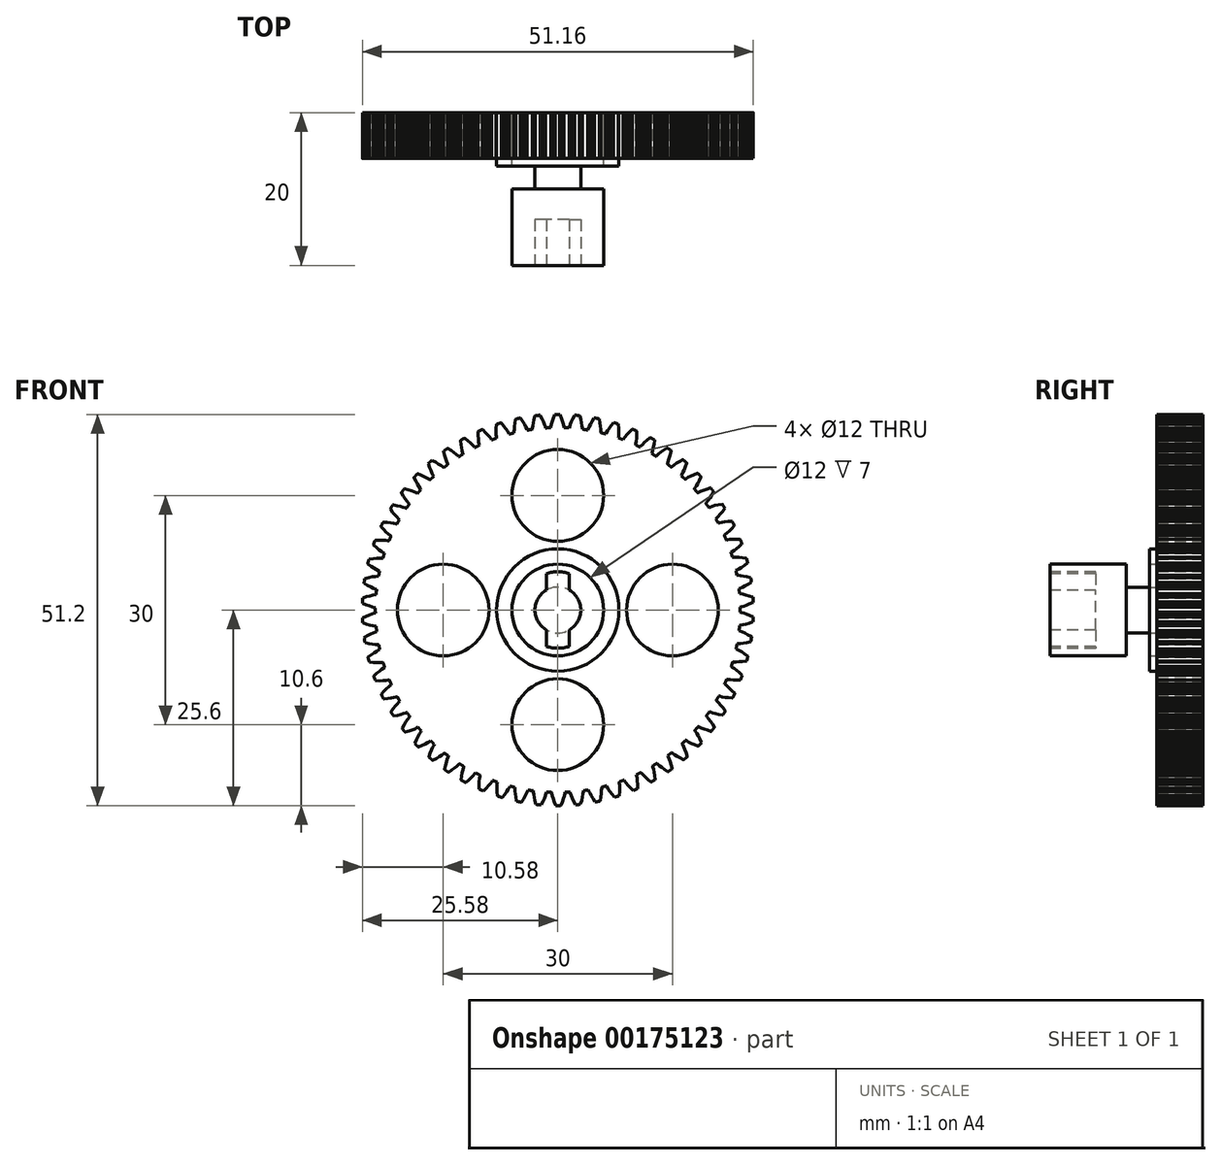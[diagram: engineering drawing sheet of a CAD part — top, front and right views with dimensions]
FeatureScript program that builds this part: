
annotation { "Feature Type Name" : "Feature", "Feature Type Description" : "" }
export const myFeature = defineFeature(function(context is Context, id is Id, definition is map)
    precondition{}
    {
        {
            var Q0;
            Q0=qCreatedBy(makeId("Front.planeOp"),FACE);
            var sketch = newSketch(context, id + "F0", { "sketchPlane" : qUnion([Q0])});
            skCircle(sketch, "E0", {"center": v(0, 0) * mm, "radius": 3 * mm});
            skCircle(sketch, "E1", {"center": v(0, 0) * mm, "radius": 6 * mm});
            skCircle(sketch, "E2", {"center": v(0, 0) * mm, "radius": 8 * mm});
            skSolve(sketch);
        }
        {
            var Q0;
            Q0=makeQuery(id+"F0.imprint","IMPRINT",FACE,{"disambiguationData":[TD([[makeQuery(id+"F0.imprint","IMPRINT",EDGE,{"derivedFrom":sQuery(id+"F0.wireOp",EDGE,"E0")}),-1.0]])]});
            var Q1;
            Q1=makeQuery(id+"F0.imprint","IMPRINT",FACE,{"disambiguationData":[TD([[makeQuery(id+"F0.imprint","IMPRINT",EDGE,{"derivedFrom":sQuery(id+"F0.wireOp",EDGE,"E0")}),1.0]])]});
            extrude(context, id + "F1", {"entities" : qUnion([Q0, Q1]), "depth" : 20 * mm});
        }
        {
            var Q0;
            Q0 = qSketchRegion(id + "F0", true);
            extrude(context, id + "F2", {"entities" : qUnion([Q0]), "operationType" : NewBodyOperationType.ADD, "depth" : 6 * mm});
        }
        {
            var Q0;
            Q0=makeQuery(id+"F0.imprint","IMPRINT",FACE,{"disambiguationData":[TD([[makeQuery(id+"F0.imprint","IMPRINT",EDGE,{"derivedFrom":sQuery(id+"F0.wireOp",EDGE,"E1")}),-1.0]])]});
            extrude(context, id + "F3", {"entities" : qUnion([Q0]), "operationType" : NewBodyOperationType.ADD, "depth" : 7 * mm});
        }
        {
            var Q0;
            Q0=makeQuery(id+"F1.opExtrude","CAP_FACE",FACE,{"disambiguationData":[OSD([sQuery(id+"F0.wireOp",EDGE,"E1")])],"isStart":false});
            var sketch = newSketch(context, id + "F4", { "sketchPlane" : qUnion([Q0])});
            skArc(sketch, "E3", {"start": v(-1.5, 2.6) * mm, "mid": v(-3, 0) * mm, "end": v(-1.5, -2.6) * mm});
            skLineSegment(sketch, "E4", {"start": v(-1.5, 4.77) * mm, "end": v(-1.5, 2.6) * mm});
            skLineSegment(sketch, "E5", {"start": v(1.5, 4.77) * mm, "end": v(1.5, 2.6) * mm});
            skArc(sketch, "E6.trimOffspring", {"start": v(1.5, -2.6) * mm, "mid": v(3, 0) * mm, "end": v(1.5, 2.6) * mm});
            skLineSegment(sketch, "E7.trimOffspring", {"start": v(-1.5, -2.6) * mm, "end": v(-1.5, -4.77) * mm});
            skLineSegment(sketch, "E8.trimOffspring", {"start": v(1.5, -2.6) * mm, "end": v(1.5, -4.77) * mm});
            skArc(sketch, "E9", {"start": v(-1.5, -4.77) * mm, "mid": v(0, -5) * mm, "end": v(1.5, -4.77) * mm});
            skArc(sketch, "E10.trimOffspring", {"start": v(1.5, 4.77) * mm, "mid": v(0, 5) * mm, "end": v(-1.5, 4.77) * mm});
            skSolve(sketch);
        }
        {
            var Q0;
            Q0=makeQuery(id+"F4.imprint","IMPRINT",FACE,{"disambiguationData":[TD([[makeQuery(id+"F4.imprint","IMPRINT",EDGE,{"derivedFrom":sQuery(id+"F4.wireOp",EDGE,"E3")}),1.0]])]});
            extrude(context, id + "F5", {"entities" : qUnion([Q0]), "operationType" : NewBodyOperationType.REMOVE, "oppositeDirection" : true, "depth" : 6 * mm});
        }
        {
            var Q0;
            Q0=qCreatedBy(makeId("Front.planeOp"),FACE);
            var sketch = newSketch(context, id + "F6", { "sketchPlane" : qUnion([Q0])});
            skLineSegment(sketch, "E11", {"start": v(18.3, 15.34) * mm, "end": v(18.43, 15.4) * mm});
            skLineSegment(sketch, "E12", {"start": v(18.43, 15.4) * mm, "end": v(18.72, 15.54) * mm});
            skLineSegment(sketch, "E13", {"start": v(18.72, 15.54) * mm, "end": v(19.07, 15.68) * mm});
            skLineSegment(sketch, "E14", {"start": v(19.07, 15.68) * mm, "end": v(19.49, 15.82) * mm});
            skLineSegment(sketch, "E15", {"start": v(19.49, 15.82) * mm, "end": v(19.96, 15.96) * mm});
            skLineSegment(sketch, "E16", {"start": v(19.96, 15.96) * mm, "end": v(20.01, 15.97) * mm});
            skArc(sketch, "E17", {"start": v(20.01, 15.97) * mm, "mid": v(20.2, 15.72) * mm, "end": v(20.4, 15.47) * mm});
            skLineSegment(sketch, "E18", {"start": v(20.4, 15.47) * mm, "end": v(20.38, 15.42) * mm});
            skLineSegment(sketch, "E19", {"start": v(20.38, 15.42) * mm, "end": v(20.13, 15) * mm});
            skLineSegment(sketch, "E20", {"start": v(20.13, 15) * mm, "end": v(19.9, 14.63) * mm});
            skLineSegment(sketch, "E21", {"start": v(19.9, 14.63) * mm, "end": v(19.67, 14.32) * mm});
            skLineSegment(sketch, "E22", {"start": v(19.67, 14.32) * mm, "end": v(19.47, 14.07) * mm});
            skLineSegment(sketch, "E23", {"start": v(19.47, 14.07) * mm, "end": v(19.37, 13.96) * mm});
            skArc(sketch, "E24", {"start": v(19.37, 13.96) * mm, "mid": v(19.56, 13.69) * mm, "end": v(19.75, 13.41) * mm});
            skLineSegment(sketch, "E25", {"start": v(19.75, 13.41) * mm, "end": v(19.9, 13.47) * mm});
            skLineSegment(sketch, "E26", {"start": v(19.9, 13.47) * mm, "end": v(20.2, 13.57) * mm});
            skLineSegment(sketch, "E27", {"start": v(20.2, 13.57) * mm, "end": v(20.56, 13.67) * mm});
            skLineSegment(sketch, "E28", {"start": v(20.56, 13.67) * mm, "end": v(20.99, 13.77) * mm});
            skLineSegment(sketch, "E29", {"start": v(20.99, 13.77) * mm, "end": v(21.47, 13.85) * mm});
            skLineSegment(sketch, "E30", {"start": v(21.47, 13.85) * mm, "end": v(21.52, 13.86) * mm});
            skArc(sketch, "E31", {"start": v(21.52, 13.86) * mm, "mid": v(21.7, 13.6) * mm, "end": v(21.86, 13.32) * mm});
            skLineSegment(sketch, "E32", {"start": v(21.86, 13.32) * mm, "end": v(21.83, 13.28) * mm});
            skLineSegment(sketch, "E33", {"start": v(21.83, 13.28) * mm, "end": v(21.54, 12.88) * mm});
            skLineSegment(sketch, "E34", {"start": v(21.54, 12.88) * mm, "end": v(21.27, 12.54) * mm});
            skLineSegment(sketch, "E35", {"start": v(21.27, 12.54) * mm, "end": v(21.02, 12.26) * mm});
            skLineSegment(sketch, "E36", {"start": v(21.02, 12.26) * mm, "end": v(20.8, 12.03) * mm});
            skLineSegment(sketch, "E37", {"start": v(20.8, 12.03) * mm, "end": v(20.68, 11.93) * mm});
            skArc(sketch, "E38", {"start": v(20.68, 11.93) * mm, "mid": v(20.85, 11.64) * mm, "end": v(21, 11.34) * mm});
            skLineSegment(sketch, "E39", {"start": v(21, 11.34) * mm, "end": v(21.15, 11.38) * mm});
            skLineSegment(sketch, "E40", {"start": v(21.15, 11.38) * mm, "end": v(21.46, 11.46) * mm});
            skLineSegment(sketch, "E41", {"start": v(21.46, 11.46) * mm, "end": v(21.84, 11.52) * mm});
            skLineSegment(sketch, "E42", {"start": v(21.84, 11.52) * mm, "end": v(22.27, 11.57) * mm});
            skLineSegment(sketch, "E43", {"start": v(22.27, 11.57) * mm, "end": v(22.77, 11.61) * mm});
            skLineSegment(sketch, "E44", {"start": v(22.77, 11.61) * mm, "end": v(22.81, 11.61) * mm});
            skArc(sketch, "E45", {"start": v(22.81, 11.61) * mm, "mid": v(22.96, 11.33) * mm, "end": v(23.1, 11.05) * mm});
            skLineSegment(sketch, "E46", {"start": v(23.1, 11.05) * mm, "end": v(23.06, 11) * mm});
            skLineSegment(sketch, "E47", {"start": v(23.06, 11) * mm, "end": v(22.73, 10.64) * mm});
            skLineSegment(sketch, "E48", {"start": v(22.73, 10.64) * mm, "end": v(22.43, 10.33) * mm});
            skLineSegment(sketch, "E49", {"start": v(22.43, 10.33) * mm, "end": v(22.15, 10.07) * mm});
            skLineSegment(sketch, "E50", {"start": v(22.15, 10.07) * mm, "end": v(21.9, 9.86) * mm});
            skLineSegment(sketch, "E51", {"start": v(21.9, 9.86) * mm, "end": v(21.78, 9.77) * mm});
            skArc(sketch, "E52", {"start": v(21.78, 9.77) * mm, "mid": v(21.92, 9.47) * mm, "end": v(22.05, 9.16) * mm});
            skLineSegment(sketch, "E53", {"start": v(22.05, 9.16) * mm, "end": v(22.2, 9.19) * mm});
            skLineSegment(sketch, "E54", {"start": v(22.2, 9.19) * mm, "end": v(22.51, 9.23) * mm});
            skLineSegment(sketch, "E55", {"start": v(22.51, 9.23) * mm, "end": v(22.9, 9.25) * mm});
            skLineSegment(sketch, "E56", {"start": v(22.9, 9.25) * mm, "end": v(23.33, 9.26) * mm});
            skLineSegment(sketch, "E57", {"start": v(23.33, 9.26) * mm, "end": v(23.82, 9.25) * mm});
            skLineSegment(sketch, "E58", {"start": v(23.82, 9.25) * mm, "end": v(23.87, 9.24) * mm});
            skArc(sketch, "E59", {"start": v(23.87, 9.24) * mm, "mid": v(23.98, 8.95) * mm, "end": v(24.1, 8.65) * mm});
            skLineSegment(sketch, "E60", {"start": v(24.1, 8.65) * mm, "end": v(24.06, 8.62) * mm});
            skLineSegment(sketch, "E61", {"start": v(24.06, 8.62) * mm, "end": v(23.7, 8.28) * mm});
            skLineSegment(sketch, "E62", {"start": v(23.7, 8.28) * mm, "end": v(23.36, 8) * mm});
            skLineSegment(sketch, "E63", {"start": v(23.36, 8) * mm, "end": v(23.05, 7.78) * mm});
            skLineSegment(sketch, "E64", {"start": v(23.05, 7.78) * mm, "end": v(22.79, 7.6) * mm});
            skLineSegment(sketch, "E65", {"start": v(22.79, 7.6) * mm, "end": v(22.66, 7.52) * mm});
            skArc(sketch, "E66", {"start": v(22.66, 7.52) * mm, "mid": v(22.76, 7.2) * mm, "end": v(22.86, 6.88) * mm});
            skLineSegment(sketch, "E67", {"start": v(22.86, 6.88) * mm, "end": v(23.01, 6.9) * mm});
            skLineSegment(sketch, "E68", {"start": v(23.01, 6.9) * mm, "end": v(23.33, 6.9) * mm});
            skLineSegment(sketch, "E69", {"start": v(23.33, 6.9) * mm, "end": v(23.7, 6.89) * mm});
            skLineSegment(sketch, "E70", {"start": v(23.7, 6.89) * mm, "end": v(24.15, 6.85) * mm});
            skLineSegment(sketch, "E71", {"start": v(24.15, 6.85) * mm, "end": v(24.64, 6.8) * mm});
            skLineSegment(sketch, "E72", {"start": v(24.64, 6.8) * mm, "end": v(24.69, 6.78) * mm});
            skArc(sketch, "E73", {"start": v(24.69, 6.78) * mm, "mid": v(24.77, 6.48) * mm, "end": v(24.85, 6.17) * mm});
            skLineSegment(sketch, "E74", {"start": v(24.85, 6.17) * mm, "end": v(24.8, 6.14) * mm});
            skLineSegment(sketch, "E75", {"start": v(24.8, 6.14) * mm, "end": v(24.41, 5.84) * mm});
            skLineSegment(sketch, "E76", {"start": v(24.41, 5.84) * mm, "end": v(24.05, 5.6) * mm});
            skLineSegment(sketch, "E77", {"start": v(24.05, 5.6) * mm, "end": v(23.72, 5.4) * mm});
            skLineSegment(sketch, "E78", {"start": v(23.72, 5.4) * mm, "end": v(23.44, 5.25) * mm});
            skLineSegment(sketch, "E79", {"start": v(23.44, 5.25) * mm, "end": v(23.3, 5.19) * mm});
            skArc(sketch, "E80", {"start": v(23.3, 5.19) * mm, "mid": v(23.37, 4.86) * mm, "end": v(23.44, 4.54) * mm});
            skLineSegment(sketch, "E81", {"start": v(23.44, 4.54) * mm, "end": v(23.6, 4.53) * mm});
            skLineSegment(sketch, "E82", {"start": v(23.6, 4.53) * mm, "end": v(23.9, 4.5) * mm});
            skLineSegment(sketch, "E83", {"start": v(23.9, 4.5) * mm, "end": v(24.29, 4.46) * mm});
            skLineSegment(sketch, "E84", {"start": v(24.29, 4.46) * mm, "end": v(24.72, 4.38) * mm});
            skLineSegment(sketch, "E85", {"start": v(24.72, 4.38) * mm, "end": v(25.2, 4.26) * mm});
            skLineSegment(sketch, "E86", {"start": v(25.2, 4.26) * mm, "end": v(25.24, 4.25) * mm});
            skArc(sketch, "E87", {"start": v(25.24, 4.25) * mm, "mid": v(25.3, 3.94) * mm, "end": v(25.34, 3.62) * mm});
            skLineSegment(sketch, "E88", {"start": v(25.34, 3.62) * mm, "end": v(25.3, 3.6) * mm});
            skLineSegment(sketch, "E89", {"start": v(25.3, 3.6) * mm, "end": v(24.88, 3.34) * mm});
            skLineSegment(sketch, "E90", {"start": v(24.88, 3.34) * mm, "end": v(24.5, 3.14) * mm});
            skLineSegment(sketch, "E91", {"start": v(24.5, 3.14) * mm, "end": v(24.15, 2.98) * mm});
            skLineSegment(sketch, "E92", {"start": v(24.15, 2.98) * mm, "end": v(23.85, 2.85) * mm});
            skLineSegment(sketch, "E93", {"start": v(23.85, 2.85) * mm, "end": v(23.7, 2.8) * mm});
            skArc(sketch, "E94", {"start": v(23.7, 2.8) * mm, "mid": v(23.75, 2.47) * mm, "end": v(23.78, 2.14) * mm});
            skLineSegment(sketch, "E95", {"start": v(23.78, 2.14) * mm, "end": v(23.93, 2.12) * mm});
            skLineSegment(sketch, "E96", {"start": v(23.93, 2.12) * mm, "end": v(24.24, 2.06) * mm});
            skLineSegment(sketch, "E97", {"start": v(24.24, 2.06) * mm, "end": v(24.61, 1.98) * mm});
            skLineSegment(sketch, "E98", {"start": v(24.61, 1.98) * mm, "end": v(25.03, 1.85) * mm});
            skLineSegment(sketch, "E99", {"start": v(25.03, 1.85) * mm, "end": v(25.5, 1.7) * mm});
            skLineSegment(sketch, "E100", {"start": v(25.5, 1.7) * mm, "end": v(25.55, 1.67) * mm});
            skArc(sketch, "E101", {"start": v(25.55, 1.67) * mm, "mid": v(25.56, 1.36) * mm, "end": v(25.58, 1.04) * mm});
            skLineSegment(sketch, "E102", {"start": v(25.58, 1.04) * mm, "end": v(25.53, 1.02) * mm});
            skLineSegment(sketch, "E103", {"start": v(25.53, 1.02) * mm, "end": v(25.09, 0.8) * mm});
            skLineSegment(sketch, "E104", {"start": v(25.09, 0.8) * mm, "end": v(24.68, 0.64) * mm});
            skLineSegment(sketch, "E105", {"start": v(24.68, 0.64) * mm, "end": v(24.32, 0.52) * mm});
            skLineSegment(sketch, "E106", {"start": v(24.32, 0.52) * mm, "end": v(24.02, 0.43) * mm});
            skLineSegment(sketch, "E107", {"start": v(24.02, 0.43) * mm, "end": v(23.87, 0.4) * mm});
            skArc(sketch, "E108", {"start": v(23.87, 0.4) * mm, "mid": v(23.87, 0.06) * mm, "end": v(23.87, -0.28) * mm});
            skLineSegment(sketch, "E109", {"start": v(23.87, -0.28) * mm, "end": v(24.02, -0.31) * mm});
            skLineSegment(sketch, "E110", {"start": v(24.02, -0.31) * mm, "end": v(24.33, -0.4) * mm});
            skLineSegment(sketch, "E111", {"start": v(24.33, -0.4) * mm, "end": v(24.68, -0.52) * mm});
            skLineSegment(sketch, "E112", {"start": v(24.68, -0.52) * mm, "end": v(25.1, -0.69) * mm});
            skLineSegment(sketch, "E113", {"start": v(25.1, -0.69) * mm, "end": v(25.54, -0.9) * mm});
            skLineSegment(sketch, "E114", {"start": v(25.54, -0.9) * mm, "end": v(25.58, -0.92) * mm});
            skArc(sketch, "E115", {"start": v(25.58, -0.92) * mm, "mid": v(25.57, -1.24) * mm, "end": v(25.55, -1.55) * mm});
            skLineSegment(sketch, "E116", {"start": v(25.55, -1.55) * mm, "end": v(25.5, -1.57) * mm});
            skLineSegment(sketch, "E117", {"start": v(25.5, -1.57) * mm, "end": v(25.04, -1.73) * mm});
            skLineSegment(sketch, "E118", {"start": v(25.04, -1.73) * mm, "end": v(24.62, -1.86) * mm});
            skLineSegment(sketch, "E119", {"start": v(24.62, -1.86) * mm, "end": v(24.25, -1.95) * mm});
            skLineSegment(sketch, "E120", {"start": v(24.25, -1.95) * mm, "end": v(23.94, -2) * mm});
            skLineSegment(sketch, "E121", {"start": v(23.94, -2) * mm, "end": v(23.79, -2.03) * mm});
            skArc(sketch, "E122", {"start": v(23.79, -2.03) * mm, "mid": v(23.76, -2.36) * mm, "end": v(23.72, -2.69) * mm});
            skLineSegment(sketch, "E123", {"start": v(23.72, -2.69) * mm, "end": v(23.86, -2.74) * mm});
            skLineSegment(sketch, "E124", {"start": v(23.86, -2.74) * mm, "end": v(24.16, -2.86) * mm});
            skLineSegment(sketch, "E125", {"start": v(24.16, -2.86) * mm, "end": v(24.5, -3.02) * mm});
            skLineSegment(sketch, "E126", {"start": v(24.5, -3.02) * mm, "end": v(24.9, -3.22) * mm});
            skLineSegment(sketch, "E127", {"start": v(24.9, -3.22) * mm, "end": v(25.32, -3.48) * mm});
            skLineSegment(sketch, "E128", {"start": v(25.32, -3.48) * mm, "end": v(25.36, -3.5) * mm});
            skArc(sketch, "E129", {"start": v(25.36, -3.5) * mm, "mid": v(25.31, -3.82) * mm, "end": v(25.27, -4.13) * mm});
            skLineSegment(sketch, "E130", {"start": v(25.27, -4.13) * mm, "end": v(25.22, -4.14) * mm});
            skLineSegment(sketch, "E131", {"start": v(25.22, -4.14) * mm, "end": v(24.74, -4.26) * mm});
            skLineSegment(sketch, "E132", {"start": v(24.74, -4.26) * mm, "end": v(24.3, -4.34) * mm});
            skLineSegment(sketch, "E133", {"start": v(24.3, -4.34) * mm, "end": v(23.93, -4.39) * mm});
            skLineSegment(sketch, "E134", {"start": v(23.93, -4.39) * mm, "end": v(23.61, -4.42) * mm});
            skLineSegment(sketch, "E135", {"start": v(23.61, -4.42) * mm, "end": v(23.46, -4.42) * mm});
            skArc(sketch, "E136", {"start": v(23.46, -4.42) * mm, "mid": v(23.4, -4.75) * mm, "end": v(23.33, -5.08) * mm});
            skLineSegment(sketch, "E137", {"start": v(23.33, -5.08) * mm, "end": v(23.47, -5.14) * mm});
            skLineSegment(sketch, "E138", {"start": v(23.47, -5.14) * mm, "end": v(23.75, -5.29) * mm});
            skLineSegment(sketch, "E139", {"start": v(23.75, -5.29) * mm, "end": v(24.07, -5.48) * mm});
            skLineSegment(sketch, "E140", {"start": v(24.07, -5.48) * mm, "end": v(24.44, -5.72) * mm});
            skLineSegment(sketch, "E141", {"start": v(24.44, -5.72) * mm, "end": v(24.84, -6.02) * mm});
            skLineSegment(sketch, "E142", {"start": v(24.84, -6.02) * mm, "end": v(24.87, -6.05) * mm});
            skArc(sketch, "E143", {"start": v(24.87, -6.05) * mm, "mid": v(24.8, -6.36) * mm, "end": v(24.72, -6.66) * mm});
            skLineSegment(sketch, "E144", {"start": v(24.72, -6.66) * mm, "end": v(24.67, -6.67) * mm});
            skLineSegment(sketch, "E145", {"start": v(24.67, -6.67) * mm, "end": v(24.18, -6.74) * mm});
            skLineSegment(sketch, "E146", {"start": v(24.18, -6.74) * mm, "end": v(23.74, -6.77) * mm});
            skLineSegment(sketch, "E147", {"start": v(23.74, -6.77) * mm, "end": v(23.36, -6.79) * mm});
            skLineSegment(sketch, "E148", {"start": v(23.36, -6.79) * mm, "end": v(23.04, -6.78) * mm});
            skLineSegment(sketch, "E149", {"start": v(23.04, -6.78) * mm, "end": v(22.9, -6.77) * mm});
            skArc(sketch, "E150", {"start": v(22.9, -6.77) * mm, "mid": v(22.8, -7.1) * mm, "end": v(22.7, -7.41) * mm});
            skLineSegment(sketch, "E151", {"start": v(22.7, -7.41) * mm, "end": v(22.82, -7.49) * mm});
            skLineSegment(sketch, "E152", {"start": v(22.82, -7.49) * mm, "end": v(23.1, -7.67) * mm});
            skLineSegment(sketch, "E153", {"start": v(23.1, -7.67) * mm, "end": v(23.4, -7.9) * mm});
            skLineSegment(sketch, "E154", {"start": v(23.4, -7.9) * mm, "end": v(23.73, -8.17) * mm});
            skLineSegment(sketch, "E155", {"start": v(23.73, -8.17) * mm, "end": v(24.1, -8.5) * mm});
            skLineSegment(sketch, "E156", {"start": v(24.1, -8.5) * mm, "end": v(24.14, -8.54) * mm});
            skArc(sketch, "E157", {"start": v(24.14, -8.54) * mm, "mid": v(24.03, -8.83) * mm, "end": v(23.92, -9.13) * mm});
            skLineSegment(sketch, "E158", {"start": v(23.92, -9.13) * mm, "end": v(23.87, -9.13) * mm});
            skLineSegment(sketch, "E159", {"start": v(23.87, -9.13) * mm, "end": v(23.37, -9.15) * mm});
            skLineSegment(sketch, "E160", {"start": v(23.37, -9.15) * mm, "end": v(22.94, -9.14) * mm});
            skLineSegment(sketch, "E161", {"start": v(22.94, -9.14) * mm, "end": v(22.56, -9.12) * mm});
            skLineSegment(sketch, "E162", {"start": v(22.56, -9.12) * mm, "end": v(22.24, -9.08) * mm});
            skLineSegment(sketch, "E163", {"start": v(22.24, -9.08) * mm, "end": v(22.1, -9.05) * mm});
            skArc(sketch, "E164", {"start": v(22.1, -9.05) * mm, "mid": v(21.96, -9.36) * mm, "end": v(21.83, -9.67) * mm});
            skLineSegment(sketch, "E165", {"start": v(21.83, -9.67) * mm, "end": v(21.95, -9.76) * mm});
            skLineSegment(sketch, "E166", {"start": v(21.95, -9.76) * mm, "end": v(22.2, -9.96) * mm});
            skLineSegment(sketch, "E167", {"start": v(22.2, -9.96) * mm, "end": v(22.48, -10.22) * mm});
            skLineSegment(sketch, "E168", {"start": v(22.48, -10.22) * mm, "end": v(22.79, -10.53) * mm});
            skLineSegment(sketch, "E169", {"start": v(22.79, -10.53) * mm, "end": v(23.12, -10.9) * mm});
            skLineSegment(sketch, "E170", {"start": v(23.12, -10.9) * mm, "end": v(23.15, -10.93) * mm});
            skArc(sketch, "E171", {"start": v(23.15, -10.93) * mm, "mid": v(23.01, -11.22) * mm, "end": v(22.87, -11.5) * mm});
            skLineSegment(sketch, "E172", {"start": v(22.87, -11.5) * mm, "end": v(22.82, -11.5) * mm});
            skLineSegment(sketch, "E173", {"start": v(22.82, -11.5) * mm, "end": v(22.33, -11.47) * mm});
            skLineSegment(sketch, "E174", {"start": v(22.33, -11.47) * mm, "end": v(21.9, -11.42) * mm});
            skLineSegment(sketch, "E175", {"start": v(21.9, -11.42) * mm, "end": v(21.52, -11.35) * mm});
            skLineSegment(sketch, "E176", {"start": v(21.52, -11.35) * mm, "end": v(21.2, -11.28) * mm});
            skLineSegment(sketch, "E177", {"start": v(21.2, -11.28) * mm, "end": v(21.06, -11.24) * mm});
            skArc(sketch, "E178", {"start": v(21.06, -11.24) * mm, "mid": v(20.9, -11.54) * mm, "end": v(20.74, -11.83) * mm});
            skLineSegment(sketch, "E179", {"start": v(20.74, -11.83) * mm, "end": v(20.85, -11.93) * mm});
            skLineSegment(sketch, "E180", {"start": v(20.85, -11.93) * mm, "end": v(21.08, -12.16) * mm});
            skLineSegment(sketch, "E181", {"start": v(21.08, -12.16) * mm, "end": v(21.33, -12.44) * mm});
            skLineSegment(sketch, "E182", {"start": v(21.33, -12.44) * mm, "end": v(21.6, -12.78) * mm});
            skLineSegment(sketch, "E183", {"start": v(21.6, -12.78) * mm, "end": v(21.9, -13.18) * mm});
            skLineSegment(sketch, "E184", {"start": v(21.9, -13.18) * mm, "end": v(21.92, -13.22) * mm});
            skArc(sketch, "E185", {"start": v(21.92, -13.22) * mm, "mid": v(21.76, -13.49) * mm, "end": v(21.59, -13.76) * mm});
            skLineSegment(sketch, "E186", {"start": v(21.59, -13.76) * mm, "end": v(21.54, -13.75) * mm});
            skLineSegment(sketch, "E187", {"start": v(21.54, -13.75) * mm, "end": v(21.05, -13.67) * mm});
            skLineSegment(sketch, "E188", {"start": v(21.05, -13.67) * mm, "end": v(20.63, -13.57) * mm});
            skLineSegment(sketch, "E189", {"start": v(20.63, -13.57) * mm, "end": v(20.26, -13.47) * mm});
            skLineSegment(sketch, "E190", {"start": v(20.26, -13.47) * mm, "end": v(19.96, -13.37) * mm});
            skLineSegment(sketch, "E191", {"start": v(19.96, -13.37) * mm, "end": v(19.82, -13.32) * mm});
            skArc(sketch, "E192", {"start": v(19.82, -13.32) * mm, "mid": v(19.63, -13.6) * mm, "end": v(19.44, -13.86) * mm});
            skLineSegment(sketch, "E193", {"start": v(19.44, -13.86) * mm, "end": v(19.54, -13.98) * mm});
            skLineSegment(sketch, "E194", {"start": v(19.54, -13.98) * mm, "end": v(19.74, -14.23) * mm});
            skLineSegment(sketch, "E195", {"start": v(19.74, -14.23) * mm, "end": v(19.96, -14.53) * mm});
            skLineSegment(sketch, "E196", {"start": v(19.96, -14.53) * mm, "end": v(20.2, -14.9) * mm});
            skLineSegment(sketch, "E197", {"start": v(20.2, -14.9) * mm, "end": v(20.45, -15.33) * mm});
            skLineSegment(sketch, "E198", {"start": v(20.45, -15.33) * mm, "end": v(20.47, -15.37) * mm});
            skArc(sketch, "E199", {"start": v(20.47, -15.37) * mm, "mid": v(20.28, -15.62) * mm, "end": v(20.09, -15.87) * mm});
            skLineSegment(sketch, "E200", {"start": v(20.09, -15.87) * mm, "end": v(20.04, -15.86) * mm});
            skLineSegment(sketch, "E201", {"start": v(20.04, -15.86) * mm, "end": v(19.56, -15.73) * mm});
            skLineSegment(sketch, "E202", {"start": v(19.56, -15.73) * mm, "end": v(19.15, -15.59) * mm});
            skLineSegment(sketch, "E203", {"start": v(19.15, -15.59) * mm, "end": v(18.8, -15.45) * mm});
            skLineSegment(sketch, "E204", {"start": v(18.8, -15.45) * mm, "end": v(18.5, -15.32) * mm});
            skLineSegment(sketch, "E205", {"start": v(18.5, -15.32) * mm, "end": v(18.37, -15.25) * mm});
            skArc(sketch, "E206", {"start": v(18.37, -15.25) * mm, "mid": v(18.15, -15.5) * mm, "end": v(17.93, -15.76) * mm});
            skLineSegment(sketch, "E207", {"start": v(17.93, -15.76) * mm, "end": v(18.02, -15.88) * mm});
            skLineSegment(sketch, "E208", {"start": v(18.02, -15.88) * mm, "end": v(18.2, -16.15) * mm});
            skLineSegment(sketch, "E209", {"start": v(18.2, -16.15) * mm, "end": v(18.39, -16.48) * mm});
            skLineSegment(sketch, "E210", {"start": v(18.39, -16.48) * mm, "end": v(18.59, -16.87) * mm});
            skLineSegment(sketch, "E211", {"start": v(18.59, -16.87) * mm, "end": v(18.8, -17.32) * mm});
            skLineSegment(sketch, "E212", {"start": v(18.8, -17.32) * mm, "end": v(18.81, -17.36) * mm});
            skArc(sketch, "E213", {"start": v(18.81, -17.36) * mm, "mid": v(18.6, -17.6) * mm, "end": v(18.38, -17.82) * mm});
            skLineSegment(sketch, "E214", {"start": v(18.38, -17.82) * mm, "end": v(18.33, -17.8) * mm});
            skLineSegment(sketch, "E215", {"start": v(18.33, -17.8) * mm, "end": v(17.87, -17.63) * mm});
            skLineSegment(sketch, "E216", {"start": v(17.87, -17.63) * mm, "end": v(17.47, -17.45) * mm});
            skLineSegment(sketch, "E217", {"start": v(17.47, -17.45) * mm, "end": v(17.13, -17.27) * mm});
            skLineSegment(sketch, "E218", {"start": v(17.13, -17.27) * mm, "end": v(16.86, -17.11) * mm});
            skLineSegment(sketch, "E219", {"start": v(16.86, -17.11) * mm, "end": v(16.73, -17.03) * mm});
            skArc(sketch, "E220", {"start": v(16.73, -17.03) * mm, "mid": v(16.5, -17.26) * mm, "end": v(16.25, -17.5) * mm});
            skLineSegment(sketch, "E221", {"start": v(16.25, -17.5) * mm, "end": v(16.32, -17.62) * mm});
            skLineSegment(sketch, "E222", {"start": v(16.32, -17.62) * mm, "end": v(16.47, -17.9) * mm});
            skLineSegment(sketch, "E223", {"start": v(16.47, -17.9) * mm, "end": v(16.63, -18.25) * mm});
            skLineSegment(sketch, "E224", {"start": v(16.63, -18.25) * mm, "end": v(16.79, -18.66) * mm});
            skLineSegment(sketch, "E225", {"start": v(16.79, -18.66) * mm, "end": v(16.95, -19.13) * mm});
            skLineSegment(sketch, "E226", {"start": v(16.95, -19.13) * mm, "end": v(16.96, -19.18) * mm});
            skArc(sketch, "E227", {"start": v(16.96, -19.18) * mm, "mid": v(16.72, -19.38) * mm, "end": v(16.48, -19.59) * mm});
            skLineSegment(sketch, "E228", {"start": v(16.48, -19.59) * mm, "end": v(16.44, -19.57) * mm});
            skLineSegment(sketch, "E229", {"start": v(16.44, -19.57) * mm, "end": v(16, -19.34) * mm});
            skLineSegment(sketch, "E230", {"start": v(16, -19.34) * mm, "end": v(15.62, -19.12) * mm});
            skLineSegment(sketch, "E231", {"start": v(15.62, -19.12) * mm, "end": v(15.3, -18.92) * mm});
            skLineSegment(sketch, "E232", {"start": v(15.3, -18.92) * mm, "end": v(15.04, -18.73) * mm});
            skLineSegment(sketch, "E233", {"start": v(15.04, -18.73) * mm, "end": v(14.92, -18.64) * mm});
            skArc(sketch, "E234", {"start": v(14.92, -18.64) * mm, "mid": v(14.66, -18.84) * mm, "end": v(14.4, -19.05) * mm});
            skLineSegment(sketch, "E235", {"start": v(14.4, -19.05) * mm, "end": v(14.46, -19.18) * mm});
            skLineSegment(sketch, "E236", {"start": v(14.46, -19.18) * mm, "end": v(14.57, -19.48) * mm});
            skLineSegment(sketch, "E237", {"start": v(14.57, -19.48) * mm, "end": v(14.7, -19.84) * mm});
            skLineSegment(sketch, "E238", {"start": v(14.7, -19.84) * mm, "end": v(14.81, -20.26) * mm});
            skLineSegment(sketch, "E239", {"start": v(14.81, -20.26) * mm, "end": v(14.92, -20.74) * mm});
            skLineSegment(sketch, "E240", {"start": v(14.92, -20.74) * mm, "end": v(14.93, -20.8) * mm});
            skArc(sketch, "E241", {"start": v(14.93, -20.8) * mm, "mid": v(14.68, -20.98) * mm, "end": v(14.41, -21.16) * mm});
            skLineSegment(sketch, "E242", {"start": v(14.41, -21.16) * mm, "end": v(14.37, -21.13) * mm});
            skLineSegment(sketch, "E243", {"start": v(14.37, -21.13) * mm, "end": v(13.96, -20.86) * mm});
            skLineSegment(sketch, "E244", {"start": v(13.96, -20.86) * mm, "end": v(13.6, -20.6) * mm});
            skLineSegment(sketch, "E245", {"start": v(13.6, -20.6) * mm, "end": v(13.3, -20.37) * mm});
            skLineSegment(sketch, "E246", {"start": v(13.3, -20.37) * mm, "end": v(13.07, -20.16) * mm});
            skLineSegment(sketch, "E247", {"start": v(13.07, -20.16) * mm, "end": v(12.96, -20.05) * mm});
            skArc(sketch, "E248", {"start": v(12.96, -20.05) * mm, "mid": v(12.68, -20.23) * mm, "end": v(12.4, -20.4) * mm});
            skLineSegment(sketch, "E249", {"start": v(12.4, -20.4) * mm, "end": v(12.44, -20.55) * mm});
            skLineSegment(sketch, "E250", {"start": v(12.44, -20.55) * mm, "end": v(12.53, -20.86) * mm});
            skLineSegment(sketch, "E251", {"start": v(12.53, -20.86) * mm, "end": v(12.61, -21.23) * mm});
            skLineSegment(sketch, "E252", {"start": v(12.61, -21.23) * mm, "end": v(12.69, -21.66) * mm});
            skLineSegment(sketch, "E253", {"start": v(12.69, -21.66) * mm, "end": v(12.75, -22.15) * mm});
            skLineSegment(sketch, "E254", {"start": v(12.75, -22.15) * mm, "end": v(12.75, -22.2) * mm});
            skArc(sketch, "E255", {"start": v(12.75, -22.2) * mm, "mid": v(12.48, -22.35) * mm, "end": v(12.2, -22.5) * mm});
            skLineSegment(sketch, "E256", {"start": v(12.2, -22.5) * mm, "end": v(12.16, -22.48) * mm});
            skLineSegment(sketch, "E257", {"start": v(12.16, -22.48) * mm, "end": v(11.77, -22.17) * mm});
            skLineSegment(sketch, "E258", {"start": v(11.77, -22.17) * mm, "end": v(11.45, -21.88) * mm});
            skLineSegment(sketch, "E259", {"start": v(11.45, -21.88) * mm, "end": v(11.18, -21.61) * mm});
            skLineSegment(sketch, "E260", {"start": v(11.18, -21.61) * mm, "end": v(10.96, -21.38) * mm});
            skLineSegment(sketch, "E261", {"start": v(10.96, -21.38) * mm, "end": v(10.86, -21.26) * mm});
            skArc(sketch, "E262", {"start": v(10.86, -21.26) * mm, "mid": v(10.57, -21.4) * mm, "end": v(10.27, -21.55) * mm});
            skLineSegment(sketch, "E263", {"start": v(10.27, -21.55) * mm, "end": v(10.3, -21.7) * mm});
            skLineSegment(sketch, "E264", {"start": v(10.3, -21.7) * mm, "end": v(10.35, -22.02) * mm});
            skLineSegment(sketch, "E265", {"start": v(10.35, -22.02) * mm, "end": v(10.4, -22.4) * mm});
            skLineSegment(sketch, "E266", {"start": v(10.4, -22.4) * mm, "end": v(10.43, -22.83) * mm});
            skLineSegment(sketch, "E267", {"start": v(10.43, -22.83) * mm, "end": v(10.44, -23.32) * mm});
            skLineSegment(sketch, "E268", {"start": v(10.44, -23.32) * mm, "end": v(10.44, -23.37) * mm});
            skArc(sketch, "E269", {"start": v(10.44, -23.37) * mm, "mid": v(10.15, -23.5) * mm, "end": v(9.86, -23.62) * mm});
            skLineSegment(sketch, "E270", {"start": v(9.86, -23.62) * mm, "end": v(9.82, -23.6) * mm});
            skLineSegment(sketch, "E271", {"start": v(9.82, -23.6) * mm, "end": v(9.47, -23.24) * mm});
            skLineSegment(sketch, "E272", {"start": v(9.47, -23.24) * mm, "end": v(9.18, -22.92) * mm});
            skLineSegment(sketch, "E273", {"start": v(9.18, -22.92) * mm, "end": v(8.93, -22.63) * mm});
            skLineSegment(sketch, "E274", {"start": v(8.93, -22.63) * mm, "end": v(8.74, -22.37) * mm});
            skLineSegment(sketch, "E275", {"start": v(8.74, -22.37) * mm, "end": v(8.66, -22.25) * mm});
            skArc(sketch, "E276", {"start": v(8.66, -22.25) * mm, "mid": v(8.35, -22.37) * mm, "end": v(8.03, -22.48) * mm});
            skLineSegment(sketch, "E277", {"start": v(8.03, -22.48) * mm, "end": v(8.05, -22.63) * mm});
            skLineSegment(sketch, "E278", {"start": v(8.05, -22.63) * mm, "end": v(8.07, -22.95) * mm});
            skLineSegment(sketch, "E279", {"start": v(8.07, -22.95) * mm, "end": v(8.08, -23.33) * mm});
            skLineSegment(sketch, "E280", {"start": v(8.08, -23.33) * mm, "end": v(8.07, -23.77) * mm});
            skLineSegment(sketch, "E281", {"start": v(8.07, -23.77) * mm, "end": v(8.03, -24.26) * mm});
            skLineSegment(sketch, "E282", {"start": v(8.03, -24.26) * mm, "end": v(8.02, -24.31) * mm});
            skArc(sketch, "E283", {"start": v(8.02, -24.31) * mm, "mid": v(7.72, -24.4) * mm, "end": v(7.42, -24.5) * mm});
            skLineSegment(sketch, "E284", {"start": v(7.42, -24.5) * mm, "end": v(7.39, -24.46) * mm});
            skLineSegment(sketch, "E285", {"start": v(7.39, -24.46) * mm, "end": v(7.07, -24.08) * mm});
            skLineSegment(sketch, "E286", {"start": v(7.07, -24.08) * mm, "end": v(6.8, -23.73) * mm});
            skLineSegment(sketch, "E287", {"start": v(6.8, -23.73) * mm, "end": v(6.6, -23.42) * mm});
            skLineSegment(sketch, "E288", {"start": v(6.6, -23.42) * mm, "end": v(6.43, -23.14) * mm});
            skLineSegment(sketch, "E289", {"start": v(6.43, -23.14) * mm, "end": v(6.36, -23.01) * mm});
            skArc(sketch, "E290", {"start": v(6.36, -23.01) * mm, "mid": v(6.04, -23.1) * mm, "end": v(5.72, -23.18) * mm});
            skLineSegment(sketch, "E291", {"start": v(5.72, -23.18) * mm, "end": v(5.72, -23.33) * mm});
            skLineSegment(sketch, "E292", {"start": v(5.72, -23.33) * mm, "end": v(5.7, -23.65) * mm});
            skLineSegment(sketch, "E293", {"start": v(5.7, -23.65) * mm, "end": v(5.68, -24.03) * mm});
            skLineSegment(sketch, "E294", {"start": v(5.68, -24.03) * mm, "end": v(5.62, -24.46) * mm});
            skLineSegment(sketch, "E295", {"start": v(5.62, -24.46) * mm, "end": v(5.53, -24.95) * mm});
            skLineSegment(sketch, "E296", {"start": v(5.53, -24.95) * mm, "end": v(5.52, -25) * mm});
            skArc(sketch, "E297", {"start": v(5.52, -25) * mm, "mid": v(5.21, -25.06) * mm, "end": v(4.9, -25.13) * mm});
            skLineSegment(sketch, "E298", {"start": v(4.9, -25.13) * mm, "end": v(4.87, -25.09) * mm});
            skLineSegment(sketch, "E299", {"start": v(4.87, -25.09) * mm, "end": v(4.6, -24.67) * mm});
            skLineSegment(sketch, "E300", {"start": v(4.6, -24.67) * mm, "end": v(4.37, -24.3) * mm});
            skLineSegment(sketch, "E301", {"start": v(4.37, -24.3) * mm, "end": v(4.2, -23.97) * mm});
            skLineSegment(sketch, "E302", {"start": v(4.2, -23.97) * mm, "end": v(4.06, -23.68) * mm});
            skLineSegment(sketch, "E303", {"start": v(4.06, -23.68) * mm, "end": v(4, -23.54) * mm});
            skArc(sketch, "E304", {"start": v(4, -23.54) * mm, "mid": v(3.67, -23.6) * mm, "end": v(3.34, -23.64) * mm});
            skLineSegment(sketch, "E305", {"start": v(3.34, -23.64) * mm, "end": v(3.33, -23.79) * mm});
            skLineSegment(sketch, "E306", {"start": v(3.33, -23.79) * mm, "end": v(3.29, -24.1) * mm});
            skLineSegment(sketch, "E307", {"start": v(3.29, -24.1) * mm, "end": v(3.22, -24.48) * mm});
            skLineSegment(sketch, "E308", {"start": v(3.22, -24.48) * mm, "end": v(3.12, -24.9) * mm});
            skLineSegment(sketch, "E309", {"start": v(3.12, -24.9) * mm, "end": v(2.98, -25.38) * mm});
            skLineSegment(sketch, "E310", {"start": v(2.98, -25.38) * mm, "end": v(2.97, -25.43) * mm});
            skArc(sketch, "E311", {"start": v(2.97, -25.43) * mm, "mid": v(2.65, -25.46) * mm, "end": v(2.34, -25.5) * mm});
            skLineSegment(sketch, "E312", {"start": v(2.34, -25.5) * mm, "end": v(2.31, -25.45) * mm});
            skLineSegment(sketch, "E313", {"start": v(2.31, -25.45) * mm, "end": v(2.08, -25.01) * mm});
            skLineSegment(sketch, "E314", {"start": v(2.08, -25.01) * mm, "end": v(1.9, -24.62) * mm});
            skLineSegment(sketch, "E315", {"start": v(1.9, -24.62) * mm, "end": v(1.75, -24.27) * mm});
            skLineSegment(sketch, "E316", {"start": v(1.75, -24.27) * mm, "end": v(1.64, -23.97) * mm});
            skLineSegment(sketch, "E317", {"start": v(1.64, -23.97) * mm, "end": v(1.6, -23.82) * mm});
            skArc(sketch, "E318", {"start": v(1.6, -23.82) * mm, "mid": v(1.27, -23.84) * mm, "end": v(0.93, -23.86) * mm});
            skLineSegment(sketch, "E319", {"start": v(0.93, -23.86) * mm, "end": v(0.9, -24) * mm});
            skLineSegment(sketch, "E320", {"start": v(0.9, -24) * mm, "end": v(0.83, -24.32) * mm});
            skLineSegment(sketch, "E321", {"start": v(0.83, -24.32) * mm, "end": v(0.73, -24.68) * mm});
            skLineSegment(sketch, "E322", {"start": v(0.73, -24.68) * mm, "end": v(0.58, -25.1) * mm});
            skLineSegment(sketch, "E323", {"start": v(0.58, -25.1) * mm, "end": v(0.4, -25.55) * mm});
            skLineSegment(sketch, "E324", {"start": v(0.4, -25.55) * mm, "end": v(0.38, -25.6) * mm});
            skArc(sketch, "E325", {"start": v(0.38, -25.6) * mm, "mid": v(0.06, -25.6) * mm, "end": v(-0.25, -25.6) * mm});
            skLineSegment(sketch, "E326", {"start": v(-0.25, -25.6) * mm, "end": v(-0.28, -25.55) * mm});
            skLineSegment(sketch, "E327", {"start": v(-0.28, -25.55) * mm, "end": v(-0.46, -25.1) * mm});
            skLineSegment(sketch, "E328", {"start": v(-0.46, -25.1) * mm, "end": v(-0.6, -24.68) * mm});
            skLineSegment(sketch, "E329", {"start": v(-0.6, -24.68) * mm, "end": v(-0.71, -24.32) * mm});
            skLineSegment(sketch, "E330", {"start": v(-0.71, -24.32) * mm, "end": v(-0.8, -24) * mm});
            skLineSegment(sketch, "E331", {"start": v(-0.8, -24) * mm, "end": v(-0.82, -23.86) * mm});
            skArc(sketch, "E332", {"start": v(-0.82, -23.86) * mm, "mid": v(-1.15, -23.85) * mm, "end": v(-1.48, -23.83) * mm});
            skLineSegment(sketch, "E333", {"start": v(-1.48, -23.83) * mm, "end": v(-1.53, -23.97) * mm});
            skLineSegment(sketch, "E334", {"start": v(-1.53, -23.97) * mm, "end": v(-1.63, -24.28) * mm});
            skLineSegment(sketch, "E335", {"start": v(-1.63, -24.28) * mm, "end": v(-1.77, -24.63) * mm});
            skLineSegment(sketch, "E336", {"start": v(-1.77, -24.63) * mm, "end": v(-1.96, -25.02) * mm});
            skLineSegment(sketch, "E337", {"start": v(-1.96, -25.02) * mm, "end": v(-2.19, -25.46) * mm});
            skLineSegment(sketch, "E338", {"start": v(-2.19, -25.46) * mm, "end": v(-2.21, -25.5) * mm});
            skArc(sketch, "E339", {"start": v(-2.21, -25.5) * mm, "mid": v(-2.53, -25.47) * mm, "end": v(-2.84, -25.44) * mm});
            skLineSegment(sketch, "E340", {"start": v(-2.84, -25.44) * mm, "end": v(-2.86, -25.4) * mm});
            skLineSegment(sketch, "E341", {"start": v(-2.86, -25.4) * mm, "end": v(-3, -24.92) * mm});
            skLineSegment(sketch, "E342", {"start": v(-3, -24.92) * mm, "end": v(-3.1, -24.5) * mm});
            skLineSegment(sketch, "E343", {"start": v(-3.1, -24.5) * mm, "end": v(-3.17, -24.12) * mm});
            skLineSegment(sketch, "E344", {"start": v(-3.17, -24.12) * mm, "end": v(-3.22, -23.8) * mm});
            skLineSegment(sketch, "E345", {"start": v(-3.22, -23.8) * mm, "end": v(-3.23, -23.66) * mm});
            skArc(sketch, "E346", {"start": v(-3.23, -23.66) * mm, "mid": v(-3.56, -23.6) * mm, "end": v(-3.89, -23.56) * mm});
            skLineSegment(sketch, "E347", {"start": v(-3.89, -23.56) * mm, "end": v(-3.94, -23.7) * mm});
            skLineSegment(sketch, "E348", {"start": v(-3.94, -23.7) * mm, "end": v(-4.08, -23.99) * mm});
            skLineSegment(sketch, "E349", {"start": v(-4.08, -23.99) * mm, "end": v(-4.26, -24.32) * mm});
            skLineSegment(sketch, "E350", {"start": v(-4.26, -24.32) * mm, "end": v(-4.48, -24.7) * mm});
            skLineSegment(sketch, "E351", {"start": v(-4.48, -24.7) * mm, "end": v(-4.75, -25.1) * mm});
            skLineSegment(sketch, "E352", {"start": v(-4.75, -25.1) * mm, "end": v(-4.78, -25.15) * mm});
            skArc(sketch, "E353", {"start": v(-4.78, -25.15) * mm, "mid": v(-5.1, -25.09) * mm, "end": v(-5.4, -25.02) * mm});
            skLineSegment(sketch, "E354", {"start": v(-5.4, -25.02) * mm, "end": v(-5.41, -24.98) * mm});
            skLineSegment(sketch, "E355", {"start": v(-5.41, -24.98) * mm, "end": v(-5.5, -24.49) * mm});
            skLineSegment(sketch, "E356", {"start": v(-5.5, -24.49) * mm, "end": v(-5.56, -24.06) * mm});
            skLineSegment(sketch, "E357", {"start": v(-5.56, -24.06) * mm, "end": v(-5.6, -23.68) * mm});
            skLineSegment(sketch, "E358", {"start": v(-5.6, -23.68) * mm, "end": v(-5.6, -23.36) * mm});
            skLineSegment(sketch, "E359", {"start": v(-5.6, -23.36) * mm, "end": v(-5.6, -23.2) * mm});
            skArc(sketch, "E360", {"start": v(-5.6, -23.2) * mm, "mid": v(-5.93, -23.13) * mm, "end": v(-6.25, -23.04) * mm});
            skLineSegment(sketch, "E361", {"start": v(-6.25, -23.04) * mm, "end": v(-6.32, -23.17) * mm});
            skLineSegment(sketch, "E362", {"start": v(-6.32, -23.17) * mm, "end": v(-6.49, -23.45) * mm});
            skLineSegment(sketch, "E363", {"start": v(-6.49, -23.45) * mm, "end": v(-6.7, -23.77) * mm});
            skLineSegment(sketch, "E364", {"start": v(-6.7, -23.77) * mm, "end": v(-6.96, -24.12) * mm});
            skLineSegment(sketch, "E365", {"start": v(-6.96, -24.12) * mm, "end": v(-7.27, -24.5) * mm});
            skLineSegment(sketch, "E366", {"start": v(-7.27, -24.5) * mm, "end": v(-7.3, -24.54) * mm});
            skArc(sketch, "E367", {"start": v(-7.3, -24.54) * mm, "mid": v(-7.6, -24.44) * mm, "end": v(-7.9, -24.35) * mm});
            skLineSegment(sketch, "E368", {"start": v(-7.9, -24.35) * mm, "end": v(-7.91, -24.3) * mm});
            skLineSegment(sketch, "E369", {"start": v(-7.91, -24.3) * mm, "end": v(-7.95, -23.8) * mm});
            skLineSegment(sketch, "E370", {"start": v(-7.95, -23.8) * mm, "end": v(-7.97, -23.37) * mm});
            skLineSegment(sketch, "E371", {"start": v(-7.97, -23.37) * mm, "end": v(-7.96, -23) * mm});
            skLineSegment(sketch, "E372", {"start": v(-7.96, -23) * mm, "end": v(-7.94, -22.67) * mm});
            skLineSegment(sketch, "E373", {"start": v(-7.94, -22.67) * mm, "end": v(-7.92, -22.52) * mm});
            skArc(sketch, "E374", {"start": v(-7.92, -22.52) * mm, "mid": v(-8.24, -22.4) * mm, "end": v(-8.55, -22.3) * mm});
            skLineSegment(sketch, "E375", {"start": v(-8.55, -22.3) * mm, "end": v(-8.63, -22.42) * mm});
            skLineSegment(sketch, "E376", {"start": v(-8.63, -22.42) * mm, "end": v(-8.82, -22.67) * mm});
            skLineSegment(sketch, "E377", {"start": v(-8.82, -22.67) * mm, "end": v(-9.07, -22.97) * mm});
            skLineSegment(sketch, "E378", {"start": v(-9.07, -22.97) * mm, "end": v(-9.36, -23.29) * mm});
            skLineSegment(sketch, "E379", {"start": v(-9.36, -23.29) * mm, "end": v(-9.71, -23.64) * mm});
            skLineSegment(sketch, "E380", {"start": v(-9.71, -23.64) * mm, "end": v(-9.75, -23.67) * mm});
            skArc(sketch, "E381", {"start": v(-9.75, -23.67) * mm, "mid": v(-10.04, -23.55) * mm, "end": v(-10.33, -23.42) * mm});
            skLineSegment(sketch, "E382", {"start": v(-10.33, -23.42) * mm, "end": v(-10.33, -23.37) * mm});
            skLineSegment(sketch, "E383", {"start": v(-10.33, -23.37) * mm, "end": v(-10.32, -22.88) * mm});
            skLineSegment(sketch, "E384", {"start": v(-10.32, -22.88) * mm, "end": v(-10.3, -22.44) * mm});
            skLineSegment(sketch, "E385", {"start": v(-10.3, -22.44) * mm, "end": v(-10.25, -22.07) * mm});
            skLineSegment(sketch, "E386", {"start": v(-10.25, -22.07) * mm, "end": v(-10.2, -21.75) * mm});
            skLineSegment(sketch, "E387", {"start": v(-10.2, -21.75) * mm, "end": v(-10.16, -21.6) * mm});
            skArc(sketch, "E388", {"start": v(-10.16, -21.6) * mm, "mid": v(-10.46, -21.46) * mm, "end": v(-10.76, -21.31) * mm});
            skLineSegment(sketch, "E389", {"start": v(-10.76, -21.31) * mm, "end": v(-10.86, -21.43) * mm});
            skLineSegment(sketch, "E390", {"start": v(-10.86, -21.43) * mm, "end": v(-11.07, -21.66) * mm});
            skLineSegment(sketch, "E391", {"start": v(-11.07, -21.66) * mm, "end": v(-11.34, -21.93) * mm});
            skLineSegment(sketch, "E392", {"start": v(-11.34, -21.93) * mm, "end": v(-11.67, -22.22) * mm});
            skLineSegment(sketch, "E393", {"start": v(-11.67, -22.22) * mm, "end": v(-12.05, -22.53) * mm});
            skLineSegment(sketch, "E394", {"start": v(-12.05, -22.53) * mm, "end": v(-12.1, -22.56) * mm});
            skArc(sketch, "E395", {"start": v(-12.1, -22.56) * mm, "mid": v(-12.37, -22.41) * mm, "end": v(-12.65, -22.26) * mm});
            skLineSegment(sketch, "E396", {"start": v(-12.65, -22.26) * mm, "end": v(-12.64, -22.2) * mm});
            skLineSegment(sketch, "E397", {"start": v(-12.64, -22.2) * mm, "end": v(-12.58, -21.72) * mm});
            skLineSegment(sketch, "E398", {"start": v(-12.58, -21.72) * mm, "end": v(-12.5, -21.29) * mm});
            skLineSegment(sketch, "E399", {"start": v(-12.5, -21.29) * mm, "end": v(-12.43, -20.92) * mm});
            skLineSegment(sketch, "E400", {"start": v(-12.43, -20.92) * mm, "end": v(-12.34, -20.6) * mm});
            skLineSegment(sketch, "E401", {"start": v(-12.34, -20.6) * mm, "end": v(-12.3, -20.47) * mm});
            skArc(sketch, "E402", {"start": v(-12.3, -20.47) * mm, "mid": v(-12.58, -20.3) * mm, "end": v(-12.86, -20.11) * mm});
            skLineSegment(sketch, "E403", {"start": v(-12.86, -20.11) * mm, "end": v(-12.97, -20.22) * mm});
            skLineSegment(sketch, "E404", {"start": v(-12.97, -20.22) * mm, "end": v(-13.2, -20.43) * mm});
            skLineSegment(sketch, "E405", {"start": v(-13.2, -20.43) * mm, "end": v(-13.5, -20.67) * mm});
            skLineSegment(sketch, "E406", {"start": v(-13.5, -20.67) * mm, "end": v(-13.86, -20.93) * mm});
            skLineSegment(sketch, "E407", {"start": v(-13.86, -20.93) * mm, "end": v(-14.27, -21.2) * mm});
            skLineSegment(sketch, "E408", {"start": v(-14.27, -21.2) * mm, "end": v(-14.31, -21.23) * mm});
            skArc(sketch, "E409", {"start": v(-14.31, -21.23) * mm, "mid": v(-14.57, -21.05) * mm, "end": v(-14.83, -20.87) * mm});
            skLineSegment(sketch, "E410", {"start": v(-14.83, -20.87) * mm, "end": v(-14.82, -20.82) * mm});
            skLineSegment(sketch, "E411", {"start": v(-14.82, -20.82) * mm, "end": v(-14.72, -20.33) * mm});
            skLineSegment(sketch, "E412", {"start": v(-14.72, -20.33) * mm, "end": v(-14.6, -19.91) * mm});
            skLineSegment(sketch, "E413", {"start": v(-14.6, -19.91) * mm, "end": v(-14.48, -19.55) * mm});
            skLineSegment(sketch, "E414", {"start": v(-14.48, -19.55) * mm, "end": v(-14.36, -19.25) * mm});
            skLineSegment(sketch, "E415", {"start": v(-14.36, -19.25) * mm, "end": v(-14.3, -19.12) * mm});
            skArc(sketch, "E416", {"start": v(-14.3, -19.12) * mm, "mid": v(-14.57, -18.91) * mm, "end": v(-14.83, -18.7) * mm});
            skLineSegment(sketch, "E417", {"start": v(-14.83, -18.7) * mm, "end": v(-14.95, -18.8) * mm});
            skLineSegment(sketch, "E418", {"start": v(-14.95, -18.8) * mm, "end": v(-15.2, -19) * mm});
            skLineSegment(sketch, "E419", {"start": v(-15.2, -19) * mm, "end": v(-15.52, -19.2) * mm});
            skLineSegment(sketch, "E420", {"start": v(-15.52, -19.2) * mm, "end": v(-15.9, -19.42) * mm});
            skLineSegment(sketch, "E421", {"start": v(-15.9, -19.42) * mm, "end": v(-16.34, -19.65) * mm});
            skLineSegment(sketch, "E422", {"start": v(-16.34, -19.65) * mm, "end": v(-16.39, -19.67) * mm});
            skArc(sketch, "E423", {"start": v(-16.39, -19.67) * mm, "mid": v(-16.63, -19.46) * mm, "end": v(-16.87, -19.26) * mm});
            skLineSegment(sketch, "E424", {"start": v(-16.87, -19.26) * mm, "end": v(-16.85, -19.2) * mm});
            skLineSegment(sketch, "E425", {"start": v(-16.85, -19.2) * mm, "end": v(-16.7, -18.74) * mm});
            skLineSegment(sketch, "E426", {"start": v(-16.7, -18.74) * mm, "end": v(-16.54, -18.33) * mm});
            skLineSegment(sketch, "E427", {"start": v(-16.54, -18.33) * mm, "end": v(-16.38, -17.99) * mm});
            skLineSegment(sketch, "E428", {"start": v(-16.38, -17.99) * mm, "end": v(-16.24, -17.7) * mm});
            skLineSegment(sketch, "E429", {"start": v(-16.24, -17.7) * mm, "end": v(-16.16, -17.57) * mm});
            skArc(sketch, "E430", {"start": v(-16.16, -17.57) * mm, "mid": v(-16.4, -17.34) * mm, "end": v(-16.65, -17.11) * mm});
            skLineSegment(sketch, "E431", {"start": v(-16.65, -17.11) * mm, "end": v(-16.77, -17.2) * mm});
            skLineSegment(sketch, "E432", {"start": v(-16.77, -17.2) * mm, "end": v(-17.05, -17.36) * mm});
            skLineSegment(sketch, "E433", {"start": v(-17.05, -17.36) * mm, "end": v(-17.39, -17.53) * mm});
            skLineSegment(sketch, "E434", {"start": v(-17.39, -17.53) * mm, "end": v(-17.79, -17.71) * mm});
            skLineSegment(sketch, "E435", {"start": v(-17.79, -17.71) * mm, "end": v(-18.25, -17.9) * mm});
            skLineSegment(sketch, "E436", {"start": v(-18.25, -17.9) * mm, "end": v(-18.3, -17.9) * mm});
            skArc(sketch, "E437", {"start": v(-18.3, -17.9) * mm, "mid": v(-18.51, -17.68) * mm, "end": v(-18.73, -17.45) * mm});
            skLineSegment(sketch, "E438", {"start": v(-18.73, -17.45) * mm, "end": v(-18.71, -17.4) * mm});
            skLineSegment(sketch, "E439", {"start": v(-18.71, -17.4) * mm, "end": v(-18.5, -16.95) * mm});
            skLineSegment(sketch, "E440", {"start": v(-18.5, -16.95) * mm, "end": v(-18.3, -16.57) * mm});
            skLineSegment(sketch, "E441", {"start": v(-18.3, -16.57) * mm, "end": v(-18.12, -16.24) * mm});
            skLineSegment(sketch, "E442", {"start": v(-18.12, -16.24) * mm, "end": v(-17.95, -15.97) * mm});
            skLineSegment(sketch, "E443", {"start": v(-17.95, -15.97) * mm, "end": v(-17.86, -15.85) * mm});
            skArc(sketch, "E444", {"start": v(-17.86, -15.85) * mm, "mid": v(-18.08, -15.6) * mm, "end": v(-18.3, -15.34) * mm});
            skLineSegment(sketch, "E445", {"start": v(-18.3, -15.34) * mm, "end": v(-18.43, -15.4) * mm});
            skLineSegment(sketch, "E446", {"start": v(-18.43, -15.4) * mm, "end": v(-18.72, -15.54) * mm});
            skLineSegment(sketch, "E447", {"start": v(-18.72, -15.54) * mm, "end": v(-19.07, -15.68) * mm});
            skLineSegment(sketch, "E448", {"start": v(-19.07, -15.68) * mm, "end": v(-19.49, -15.82) * mm});
            skLineSegment(sketch, "E449", {"start": v(-19.49, -15.82) * mm, "end": v(-19.96, -15.96) * mm});
            skLineSegment(sketch, "E450", {"start": v(-19.96, -15.96) * mm, "end": v(-20.01, -15.97) * mm});
            skArc(sketch, "E451", {"start": v(-20.01, -15.97) * mm, "mid": v(-20.2, -15.72) * mm, "end": v(-20.4, -15.47) * mm});
            skLineSegment(sketch, "E452", {"start": v(-20.4, -15.47) * mm, "end": v(-20.38, -15.42) * mm});
            skLineSegment(sketch, "E453", {"start": v(-20.38, -15.42) * mm, "end": v(-20.13, -15) * mm});
            skLineSegment(sketch, "E454", {"start": v(-20.13, -15) * mm, "end": v(-19.9, -14.63) * mm});
            skLineSegment(sketch, "E455", {"start": v(-19.9, -14.63) * mm, "end": v(-19.67, -14.32) * mm});
            skLineSegment(sketch, "E456", {"start": v(-19.67, -14.32) * mm, "end": v(-19.47, -14.07) * mm});
            skLineSegment(sketch, "E457", {"start": v(-19.47, -14.07) * mm, "end": v(-19.37, -13.96) * mm});
            skArc(sketch, "E458", {"start": v(-19.37, -13.96) * mm, "mid": v(-19.56, -13.69) * mm, "end": v(-19.75, -13.41) * mm});
            skLineSegment(sketch, "E459", {"start": v(-19.75, -13.41) * mm, "end": v(-19.9, -13.47) * mm});
            skLineSegment(sketch, "E460", {"start": v(-19.9, -13.47) * mm, "end": v(-20.2, -13.57) * mm});
            skLineSegment(sketch, "E461", {"start": v(-20.2, -13.57) * mm, "end": v(-20.56, -13.67) * mm});
            skLineSegment(sketch, "E462", {"start": v(-20.56, -13.67) * mm, "end": v(-20.99, -13.77) * mm});
            skLineSegment(sketch, "E463", {"start": v(-20.99, -13.77) * mm, "end": v(-21.47, -13.85) * mm});
            skLineSegment(sketch, "E464", {"start": v(-21.47, -13.85) * mm, "end": v(-21.52, -13.86) * mm});
            skArc(sketch, "E465", {"start": v(-21.52, -13.86) * mm, "mid": v(-21.7, -13.6) * mm, "end": v(-21.86, -13.32) * mm});
            skLineSegment(sketch, "E466", {"start": v(-21.86, -13.32) * mm, "end": v(-21.83, -13.28) * mm});
            skLineSegment(sketch, "E467", {"start": v(-21.83, -13.28) * mm, "end": v(-21.54, -12.88) * mm});
            skLineSegment(sketch, "E468", {"start": v(-21.54, -12.88) * mm, "end": v(-21.27, -12.54) * mm});
            skLineSegment(sketch, "E469", {"start": v(-21.27, -12.54) * mm, "end": v(-21.02, -12.26) * mm});
            skLineSegment(sketch, "E470", {"start": v(-21.02, -12.26) * mm, "end": v(-20.8, -12.03) * mm});
            skLineSegment(sketch, "E471", {"start": v(-20.8, -12.03) * mm, "end": v(-20.68, -11.93) * mm});
            skArc(sketch, "E472", {"start": v(-20.68, -11.93) * mm, "mid": v(-20.85, -11.64) * mm, "end": v(-21, -11.34) * mm});
            skLineSegment(sketch, "E473", {"start": v(-21, -11.34) * mm, "end": v(-21.15, -11.38) * mm});
            skLineSegment(sketch, "E474", {"start": v(-21.15, -11.38) * mm, "end": v(-21.46, -11.46) * mm});
            skLineSegment(sketch, "E475", {"start": v(-21.46, -11.46) * mm, "end": v(-21.84, -11.52) * mm});
            skLineSegment(sketch, "E476", {"start": v(-21.84, -11.52) * mm, "end": v(-22.27, -11.57) * mm});
            skLineSegment(sketch, "E477", {"start": v(-22.27, -11.57) * mm, "end": v(-22.77, -11.61) * mm});
            skLineSegment(sketch, "E478", {"start": v(-22.77, -11.61) * mm, "end": v(-22.81, -11.61) * mm});
            skArc(sketch, "E479", {"start": v(-22.81, -11.61) * mm, "mid": v(-22.96, -11.33) * mm, "end": v(-23.1, -11.05) * mm});
            skLineSegment(sketch, "E480", {"start": v(-23.1, -11.05) * mm, "end": v(-23.06, -11) * mm});
            skLineSegment(sketch, "E481", {"start": v(-23.06, -11) * mm, "end": v(-22.73, -10.64) * mm});
            skLineSegment(sketch, "E482", {"start": v(-22.73, -10.64) * mm, "end": v(-22.43, -10.33) * mm});
            skLineSegment(sketch, "E483", {"start": v(-22.43, -10.33) * mm, "end": v(-22.15, -10.07) * mm});
            skLineSegment(sketch, "E484", {"start": v(-22.15, -10.07) * mm, "end": v(-21.9, -9.86) * mm});
            skLineSegment(sketch, "E485", {"start": v(-21.9, -9.86) * mm, "end": v(-21.78, -9.77) * mm});
            skArc(sketch, "E486", {"start": v(-21.78, -9.77) * mm, "mid": v(-21.92, -9.47) * mm, "end": v(-22.05, -9.16) * mm});
            skLineSegment(sketch, "E487", {"start": v(-22.05, -9.16) * mm, "end": v(-22.2, -9.19) * mm});
            skLineSegment(sketch, "E488", {"start": v(-22.2, -9.19) * mm, "end": v(-22.51, -9.23) * mm});
            skLineSegment(sketch, "E489", {"start": v(-22.51, -9.23) * mm, "end": v(-22.9, -9.25) * mm});
            skLineSegment(sketch, "E490", {"start": v(-22.9, -9.25) * mm, "end": v(-23.33, -9.26) * mm});
            skLineSegment(sketch, "E491", {"start": v(-23.33, -9.26) * mm, "end": v(-23.82, -9.25) * mm});
            skLineSegment(sketch, "E492", {"start": v(-23.82, -9.25) * mm, "end": v(-23.87, -9.24) * mm});
            skArc(sketch, "E493", {"start": v(-23.87, -9.24) * mm, "mid": v(-23.98, -8.95) * mm, "end": v(-24.1, -8.65) * mm});
            skLineSegment(sketch, "E494", {"start": v(-24.1, -8.65) * mm, "end": v(-24.06, -8.62) * mm});
            skLineSegment(sketch, "E495", {"start": v(-24.06, -8.62) * mm, "end": v(-23.7, -8.28) * mm});
            skLineSegment(sketch, "E496", {"start": v(-23.7, -8.28) * mm, "end": v(-23.36, -8) * mm});
            skLineSegment(sketch, "E497", {"start": v(-23.36, -8) * mm, "end": v(-23.05, -7.78) * mm});
            skLineSegment(sketch, "E498", {"start": v(-23.05, -7.78) * mm, "end": v(-22.79, -7.6) * mm});
            skLineSegment(sketch, "E499", {"start": v(-22.79, -7.6) * mm, "end": v(-22.66, -7.52) * mm});
            skArc(sketch, "E500", {"start": v(-22.66, -7.52) * mm, "mid": v(-22.76, -7.2) * mm, "end": v(-22.86, -6.88) * mm});
            skLineSegment(sketch, "E501", {"start": v(-22.86, -6.88) * mm, "end": v(-23.01, -6.9) * mm});
            skLineSegment(sketch, "E502", {"start": v(-23.01, -6.9) * mm, "end": v(-23.33, -6.9) * mm});
            skLineSegment(sketch, "E503", {"start": v(-23.33, -6.9) * mm, "end": v(-23.7, -6.89) * mm});
            skLineSegment(sketch, "E504", {"start": v(-23.7, -6.89) * mm, "end": v(-24.15, -6.85) * mm});
            skLineSegment(sketch, "E505", {"start": v(-24.15, -6.85) * mm, "end": v(-24.64, -6.8) * mm});
            skLineSegment(sketch, "E506", {"start": v(-24.64, -6.8) * mm, "end": v(-24.69, -6.78) * mm});
            skArc(sketch, "E507", {"start": v(-24.69, -6.78) * mm, "mid": v(-24.77, -6.48) * mm, "end": v(-24.85, -6.17) * mm});
            skLineSegment(sketch, "E508", {"start": v(-24.85, -6.17) * mm, "end": v(-24.8, -6.14) * mm});
            skLineSegment(sketch, "E509", {"start": v(-24.8, -6.14) * mm, "end": v(-24.41, -5.84) * mm});
            skLineSegment(sketch, "E510", {"start": v(-24.41, -5.84) * mm, "end": v(-24.05, -5.6) * mm});
            skLineSegment(sketch, "E511", {"start": v(-24.05, -5.6) * mm, "end": v(-23.72, -5.4) * mm});
            skLineSegment(sketch, "E512", {"start": v(-23.72, -5.4) * mm, "end": v(-23.44, -5.25) * mm});
            skLineSegment(sketch, "E513", {"start": v(-23.44, -5.25) * mm, "end": v(-23.3, -5.19) * mm});
            skArc(sketch, "E514", {"start": v(-23.3, -5.19) * mm, "mid": v(-23.37, -4.86) * mm, "end": v(-23.44, -4.54) * mm});
            skLineSegment(sketch, "E515", {"start": v(-23.44, -4.54) * mm, "end": v(-23.6, -4.53) * mm});
            skLineSegment(sketch, "E516", {"start": v(-23.6, -4.53) * mm, "end": v(-23.9, -4.5) * mm});
            skLineSegment(sketch, "E517", {"start": v(-23.9, -4.5) * mm, "end": v(-24.29, -4.46) * mm});
            skLineSegment(sketch, "E518", {"start": v(-24.29, -4.46) * mm, "end": v(-24.72, -4.38) * mm});
            skLineSegment(sketch, "E519", {"start": v(-24.72, -4.38) * mm, "end": v(-25.2, -4.26) * mm});
            skLineSegment(sketch, "E520", {"start": v(-25.2, -4.26) * mm, "end": v(-25.24, -4.25) * mm});
            skArc(sketch, "E521", {"start": v(-25.24, -4.25) * mm, "mid": v(-25.3, -3.94) * mm, "end": v(-25.34, -3.62) * mm});
            skLineSegment(sketch, "E522", {"start": v(-25.34, -3.62) * mm, "end": v(-25.3, -3.6) * mm});
            skLineSegment(sketch, "E523", {"start": v(-25.3, -3.6) * mm, "end": v(-24.88, -3.34) * mm});
            skLineSegment(sketch, "E524", {"start": v(-24.88, -3.34) * mm, "end": v(-24.5, -3.14) * mm});
            skLineSegment(sketch, "E525", {"start": v(-24.5, -3.14) * mm, "end": v(-24.15, -2.98) * mm});
            skLineSegment(sketch, "E526", {"start": v(-24.15, -2.98) * mm, "end": v(-23.85, -2.85) * mm});
            skLineSegment(sketch, "E527", {"start": v(-23.85, -2.85) * mm, "end": v(-23.7, -2.8) * mm});
            skArc(sketch, "E528", {"start": v(-23.7, -2.8) * mm, "mid": v(-23.75, -2.47) * mm, "end": v(-23.78, -2.14) * mm});
            skLineSegment(sketch, "E529", {"start": v(-23.78, -2.14) * mm, "end": v(-23.93, -2.12) * mm});
            skLineSegment(sketch, "E530", {"start": v(-23.93, -2.12) * mm, "end": v(-24.24, -2.06) * mm});
            skLineSegment(sketch, "E531", {"start": v(-24.24, -2.06) * mm, "end": v(-24.61, -1.98) * mm});
            skLineSegment(sketch, "E532", {"start": v(-24.61, -1.98) * mm, "end": v(-25.03, -1.85) * mm});
            skLineSegment(sketch, "E533", {"start": v(-25.03, -1.85) * mm, "end": v(-25.5, -1.7) * mm});
            skLineSegment(sketch, "E534", {"start": v(-25.5, -1.7) * mm, "end": v(-25.55, -1.67) * mm});
            skArc(sketch, "E535", {"start": v(-25.55, -1.67) * mm, "mid": v(-25.56, -1.36) * mm, "end": v(-25.58, -1.04) * mm});
            skLineSegment(sketch, "E536", {"start": v(-25.58, -1.04) * mm, "end": v(-25.53, -1.02) * mm});
            skLineSegment(sketch, "E537", {"start": v(-25.53, -1.02) * mm, "end": v(-25.09, -0.8) * mm});
            skLineSegment(sketch, "E538", {"start": v(-25.09, -0.8) * mm, "end": v(-24.68, -0.64) * mm});
            skLineSegment(sketch, "E539", {"start": v(-24.68, -0.64) * mm, "end": v(-24.32, -0.52) * mm});
            skLineSegment(sketch, "E540", {"start": v(-24.32, -0.52) * mm, "end": v(-24.02, -0.43) * mm});
            skLineSegment(sketch, "E541", {"start": v(-24.02, -0.43) * mm, "end": v(-23.87, -0.4) * mm});
            skArc(sketch, "E542", {"start": v(-23.87, -0.4) * mm, "mid": v(-23.87, -0.06) * mm, "end": v(-23.87, 0.28) * mm});
            skLineSegment(sketch, "E543", {"start": v(-23.87, 0.28) * mm, "end": v(-24.02, 0.31) * mm});
            skLineSegment(sketch, "E544", {"start": v(-24.02, 0.31) * mm, "end": v(-24.33, 0.4) * mm});
            skLineSegment(sketch, "E545", {"start": v(-24.33, 0.4) * mm, "end": v(-24.68, 0.52) * mm});
            skLineSegment(sketch, "E546", {"start": v(-24.68, 0.52) * mm, "end": v(-25.1, 0.69) * mm});
            skLineSegment(sketch, "E547", {"start": v(-25.1, 0.69) * mm, "end": v(-25.54, 0.9) * mm});
            skLineSegment(sketch, "E548", {"start": v(-25.54, 0.9) * mm, "end": v(-25.58, 0.92) * mm});
            skArc(sketch, "E549", {"start": v(-25.58, 0.92) * mm, "mid": v(-25.57, 1.24) * mm, "end": v(-25.55, 1.55) * mm});
            skLineSegment(sketch, "E550", {"start": v(-25.55, 1.55) * mm, "end": v(-25.5, 1.57) * mm});
            skLineSegment(sketch, "E551", {"start": v(-25.5, 1.57) * mm, "end": v(-25.04, 1.73) * mm});
            skLineSegment(sketch, "E552", {"start": v(-25.04, 1.73) * mm, "end": v(-24.62, 1.86) * mm});
            skLineSegment(sketch, "E553", {"start": v(-24.62, 1.86) * mm, "end": v(-24.25, 1.95) * mm});
            skLineSegment(sketch, "E554", {"start": v(-24.25, 1.95) * mm, "end": v(-23.94, 2) * mm});
            skLineSegment(sketch, "E555", {"start": v(-23.94, 2) * mm, "end": v(-23.79, 2.03) * mm});
            skArc(sketch, "E556", {"start": v(-23.79, 2.03) * mm, "mid": v(-23.76, 2.36) * mm, "end": v(-23.72, 2.69) * mm});
            skLineSegment(sketch, "E557", {"start": v(-23.72, 2.69) * mm, "end": v(-23.86, 2.74) * mm});
            skLineSegment(sketch, "E558", {"start": v(-23.86, 2.74) * mm, "end": v(-24.16, 2.86) * mm});
            skLineSegment(sketch, "E559", {"start": v(-24.16, 2.86) * mm, "end": v(-24.5, 3.02) * mm});
            skLineSegment(sketch, "E560", {"start": v(-24.5, 3.02) * mm, "end": v(-24.9, 3.22) * mm});
            skLineSegment(sketch, "E561", {"start": v(-24.9, 3.22) * mm, "end": v(-25.32, 3.48) * mm});
            skLineSegment(sketch, "E562", {"start": v(-25.32, 3.48) * mm, "end": v(-25.36, 3.5) * mm});
            skArc(sketch, "E563", {"start": v(-25.36, 3.5) * mm, "mid": v(-25.31, 3.82) * mm, "end": v(-25.27, 4.13) * mm});
            skLineSegment(sketch, "E564", {"start": v(-25.27, 4.13) * mm, "end": v(-25.22, 4.14) * mm});
            skLineSegment(sketch, "E565", {"start": v(-25.22, 4.14) * mm, "end": v(-24.74, 4.26) * mm});
            skLineSegment(sketch, "E566", {"start": v(-24.74, 4.26) * mm, "end": v(-24.3, 4.34) * mm});
            skLineSegment(sketch, "E567", {"start": v(-24.3, 4.34) * mm, "end": v(-23.93, 4.39) * mm});
            skLineSegment(sketch, "E568", {"start": v(-23.93, 4.39) * mm, "end": v(-23.61, 4.42) * mm});
            skLineSegment(sketch, "E569", {"start": v(-23.61, 4.42) * mm, "end": v(-23.46, 4.42) * mm});
            skArc(sketch, "E570", {"start": v(-23.46, 4.42) * mm, "mid": v(-23.4, 4.75) * mm, "end": v(-23.33, 5.08) * mm});
            skLineSegment(sketch, "E571", {"start": v(-23.33, 5.08) * mm, "end": v(-23.47, 5.14) * mm});
            skLineSegment(sketch, "E572", {"start": v(-23.47, 5.14) * mm, "end": v(-23.75, 5.29) * mm});
            skLineSegment(sketch, "E573", {"start": v(-23.75, 5.29) * mm, "end": v(-24.07, 5.48) * mm});
            skLineSegment(sketch, "E574", {"start": v(-24.07, 5.48) * mm, "end": v(-24.44, 5.72) * mm});
            skLineSegment(sketch, "E575", {"start": v(-24.44, 5.72) * mm, "end": v(-24.84, 6.02) * mm});
            skLineSegment(sketch, "E576", {"start": v(-24.84, 6.02) * mm, "end": v(-24.87, 6.05) * mm});
            skArc(sketch, "E577", {"start": v(-24.87, 6.05) * mm, "mid": v(-24.8, 6.36) * mm, "end": v(-24.72, 6.66) * mm});
            skLineSegment(sketch, "E578", {"start": v(-24.72, 6.66) * mm, "end": v(-24.67, 6.67) * mm});
            skLineSegment(sketch, "E579", {"start": v(-24.67, 6.67) * mm, "end": v(-24.18, 6.74) * mm});
            skLineSegment(sketch, "E580", {"start": v(-24.18, 6.74) * mm, "end": v(-23.74, 6.77) * mm});
            skLineSegment(sketch, "E581", {"start": v(-23.74, 6.77) * mm, "end": v(-23.36, 6.79) * mm});
            skLineSegment(sketch, "E582", {"start": v(-23.36, 6.79) * mm, "end": v(-23.04, 6.78) * mm});
            skLineSegment(sketch, "E583", {"start": v(-23.04, 6.78) * mm, "end": v(-22.9, 6.77) * mm});
            skArc(sketch, "E584", {"start": v(-22.9, 6.77) * mm, "mid": v(-22.8, 7.1) * mm, "end": v(-22.7, 7.41) * mm});
            skLineSegment(sketch, "E585", {"start": v(-22.7, 7.41) * mm, "end": v(-22.82, 7.49) * mm});
            skLineSegment(sketch, "E586", {"start": v(-22.82, 7.49) * mm, "end": v(-23.1, 7.67) * mm});
            skLineSegment(sketch, "E587", {"start": v(-23.1, 7.67) * mm, "end": v(-23.4, 7.9) * mm});
            skLineSegment(sketch, "E588", {"start": v(-23.4, 7.9) * mm, "end": v(-23.73, 8.17) * mm});
            skLineSegment(sketch, "E589", {"start": v(-23.73, 8.17) * mm, "end": v(-24.1, 8.5) * mm});
            skLineSegment(sketch, "E590", {"start": v(-24.1, 8.5) * mm, "end": v(-24.14, 8.54) * mm});
            skArc(sketch, "E591", {"start": v(-24.14, 8.54) * mm, "mid": v(-24.03, 8.83) * mm, "end": v(-23.92, 9.13) * mm});
            skLineSegment(sketch, "E592", {"start": v(-23.92, 9.13) * mm, "end": v(-23.87, 9.13) * mm});
            skLineSegment(sketch, "E593", {"start": v(-23.87, 9.13) * mm, "end": v(-23.37, 9.15) * mm});
            skLineSegment(sketch, "E594", {"start": v(-23.37, 9.15) * mm, "end": v(-22.94, 9.14) * mm});
            skLineSegment(sketch, "E595", {"start": v(-22.94, 9.14) * mm, "end": v(-22.56, 9.12) * mm});
            skLineSegment(sketch, "E596", {"start": v(-22.56, 9.12) * mm, "end": v(-22.24, 9.08) * mm});
            skLineSegment(sketch, "E597", {"start": v(-22.24, 9.08) * mm, "end": v(-22.1, 9.05) * mm});
            skArc(sketch, "E598", {"start": v(-22.1, 9.05) * mm, "mid": v(-21.96, 9.36) * mm, "end": v(-21.83, 9.67) * mm});
            skLineSegment(sketch, "E599", {"start": v(-21.83, 9.67) * mm, "end": v(-21.95, 9.76) * mm});
            skLineSegment(sketch, "E600", {"start": v(-21.95, 9.76) * mm, "end": v(-22.2, 9.96) * mm});
            skLineSegment(sketch, "E601", {"start": v(-22.2, 9.96) * mm, "end": v(-22.48, 10.22) * mm});
            skLineSegment(sketch, "E602", {"start": v(-22.48, 10.22) * mm, "end": v(-22.79, 10.53) * mm});
            skLineSegment(sketch, "E603", {"start": v(-22.79, 10.53) * mm, "end": v(-23.12, 10.9) * mm});
            skLineSegment(sketch, "E604", {"start": v(-23.12, 10.9) * mm, "end": v(-23.15, 10.93) * mm});
            skArc(sketch, "E605", {"start": v(-23.15, 10.93) * mm, "mid": v(-23.01, 11.22) * mm, "end": v(-22.87, 11.5) * mm});
            skLineSegment(sketch, "E606", {"start": v(-22.87, 11.5) * mm, "end": v(-22.82, 11.5) * mm});
            skLineSegment(sketch, "E607", {"start": v(-22.82, 11.5) * mm, "end": v(-22.33, 11.47) * mm});
            skLineSegment(sketch, "E608", {"start": v(-22.33, 11.47) * mm, "end": v(-21.9, 11.42) * mm});
            skLineSegment(sketch, "E609", {"start": v(-21.9, 11.42) * mm, "end": v(-21.52, 11.35) * mm});
            skLineSegment(sketch, "E610", {"start": v(-21.52, 11.35) * mm, "end": v(-21.2, 11.28) * mm});
            skLineSegment(sketch, "E611", {"start": v(-21.2, 11.28) * mm, "end": v(-21.06, 11.24) * mm});
            skArc(sketch, "E612", {"start": v(-21.06, 11.24) * mm, "mid": v(-20.9, 11.54) * mm, "end": v(-20.74, 11.83) * mm});
            skLineSegment(sketch, "E613", {"start": v(-20.74, 11.83) * mm, "end": v(-20.85, 11.93) * mm});
            skLineSegment(sketch, "E614", {"start": v(-20.85, 11.93) * mm, "end": v(-21.08, 12.16) * mm});
            skLineSegment(sketch, "E615", {"start": v(-21.08, 12.16) * mm, "end": v(-21.33, 12.44) * mm});
            skLineSegment(sketch, "E616", {"start": v(-21.33, 12.44) * mm, "end": v(-21.6, 12.78) * mm});
            skLineSegment(sketch, "E617", {"start": v(-21.6, 12.78) * mm, "end": v(-21.9, 13.18) * mm});
            skLineSegment(sketch, "E618", {"start": v(-21.9, 13.18) * mm, "end": v(-21.92, 13.22) * mm});
            skArc(sketch, "E619", {"start": v(-21.92, 13.22) * mm, "mid": v(-21.76, 13.49) * mm, "end": v(-21.59, 13.76) * mm});
            skLineSegment(sketch, "E620", {"start": v(-21.59, 13.76) * mm, "end": v(-21.54, 13.75) * mm});
            skLineSegment(sketch, "E621", {"start": v(-21.54, 13.75) * mm, "end": v(-21.05, 13.67) * mm});
            skLineSegment(sketch, "E622", {"start": v(-21.05, 13.67) * mm, "end": v(-20.63, 13.57) * mm});
            skLineSegment(sketch, "E623", {"start": v(-20.63, 13.57) * mm, "end": v(-20.26, 13.47) * mm});
            skLineSegment(sketch, "E624", {"start": v(-20.26, 13.47) * mm, "end": v(-19.96, 13.37) * mm});
            skLineSegment(sketch, "E625", {"start": v(-19.96, 13.37) * mm, "end": v(-19.82, 13.32) * mm});
            skArc(sketch, "E626", {"start": v(-19.82, 13.32) * mm, "mid": v(-19.63, 13.6) * mm, "end": v(-19.44, 13.86) * mm});
            skLineSegment(sketch, "E627", {"start": v(-19.44, 13.86) * mm, "end": v(-19.54, 13.98) * mm});
            skLineSegment(sketch, "E628", {"start": v(-19.54, 13.98) * mm, "end": v(-19.74, 14.23) * mm});
            skLineSegment(sketch, "E629", {"start": v(-19.74, 14.23) * mm, "end": v(-19.96, 14.53) * mm});
            skLineSegment(sketch, "E630", {"start": v(-19.96, 14.53) * mm, "end": v(-20.2, 14.9) * mm});
            skLineSegment(sketch, "E631", {"start": v(-20.2, 14.9) * mm, "end": v(-20.45, 15.33) * mm});
            skLineSegment(sketch, "E632", {"start": v(-20.45, 15.33) * mm, "end": v(-20.47, 15.37) * mm});
            skArc(sketch, "E633", {"start": v(-20.47, 15.37) * mm, "mid": v(-20.28, 15.62) * mm, "end": v(-20.09, 15.87) * mm});
            skLineSegment(sketch, "E634", {"start": v(-20.09, 15.87) * mm, "end": v(-20.04, 15.86) * mm});
            skLineSegment(sketch, "E635", {"start": v(-20.04, 15.86) * mm, "end": v(-19.56, 15.73) * mm});
            skLineSegment(sketch, "E636", {"start": v(-19.56, 15.73) * mm, "end": v(-19.15, 15.59) * mm});
            skLineSegment(sketch, "E637", {"start": v(-19.15, 15.59) * mm, "end": v(-18.8, 15.45) * mm});
            skLineSegment(sketch, "E638", {"start": v(-18.8, 15.45) * mm, "end": v(-18.5, 15.32) * mm});
            skLineSegment(sketch, "E639", {"start": v(-18.5, 15.32) * mm, "end": v(-18.37, 15.25) * mm});
            skArc(sketch, "E640", {"start": v(-18.37, 15.25) * mm, "mid": v(-18.15, 15.5) * mm, "end": v(-17.93, 15.76) * mm});
            skLineSegment(sketch, "E641", {"start": v(-17.93, 15.76) * mm, "end": v(-18.02, 15.88) * mm});
            skLineSegment(sketch, "E642", {"start": v(-18.02, 15.88) * mm, "end": v(-18.2, 16.15) * mm});
            skLineSegment(sketch, "E643", {"start": v(-18.2, 16.15) * mm, "end": v(-18.39, 16.48) * mm});
            skLineSegment(sketch, "E644", {"start": v(-18.39, 16.48) * mm, "end": v(-18.59, 16.87) * mm});
            skLineSegment(sketch, "E645", {"start": v(-18.59, 16.87) * mm, "end": v(-18.8, 17.32) * mm});
            skLineSegment(sketch, "E646", {"start": v(-18.8, 17.32) * mm, "end": v(-18.81, 17.36) * mm});
            skArc(sketch, "E647", {"start": v(-18.81, 17.36) * mm, "mid": v(-18.6, 17.6) * mm, "end": v(-18.38, 17.82) * mm});
            skLineSegment(sketch, "E648", {"start": v(-18.38, 17.82) * mm, "end": v(-18.33, 17.8) * mm});
            skLineSegment(sketch, "E649", {"start": v(-18.33, 17.8) * mm, "end": v(-17.87, 17.63) * mm});
            skLineSegment(sketch, "E650", {"start": v(-17.87, 17.63) * mm, "end": v(-17.47, 17.45) * mm});
            skLineSegment(sketch, "E651", {"start": v(-17.47, 17.45) * mm, "end": v(-17.13, 17.27) * mm});
            skLineSegment(sketch, "E652", {"start": v(-17.13, 17.27) * mm, "end": v(-16.86, 17.11) * mm});
            skLineSegment(sketch, "E653", {"start": v(-16.86, 17.11) * mm, "end": v(-16.73, 17.03) * mm});
            skArc(sketch, "E654", {"start": v(-16.73, 17.03) * mm, "mid": v(-16.5, 17.26) * mm, "end": v(-16.25, 17.5) * mm});
            skLineSegment(sketch, "E655", {"start": v(-16.25, 17.5) * mm, "end": v(-16.32, 17.62) * mm});
            skLineSegment(sketch, "E656", {"start": v(-16.32, 17.62) * mm, "end": v(-16.47, 17.9) * mm});
            skLineSegment(sketch, "E657", {"start": v(-16.47, 17.9) * mm, "end": v(-16.63, 18.25) * mm});
            skLineSegment(sketch, "E658", {"start": v(-16.63, 18.25) * mm, "end": v(-16.79, 18.66) * mm});
            skLineSegment(sketch, "E659", {"start": v(-16.79, 18.66) * mm, "end": v(-16.95, 19.13) * mm});
            skLineSegment(sketch, "E660", {"start": v(-16.95, 19.13) * mm, "end": v(-16.96, 19.18) * mm});
            skArc(sketch, "E661", {"start": v(-16.96, 19.18) * mm, "mid": v(-16.72, 19.38) * mm, "end": v(-16.48, 19.59) * mm});
            skLineSegment(sketch, "E662", {"start": v(-16.48, 19.59) * mm, "end": v(-16.44, 19.57) * mm});
            skLineSegment(sketch, "E663", {"start": v(-16.44, 19.57) * mm, "end": v(-16, 19.34) * mm});
            skLineSegment(sketch, "E664", {"start": v(-16, 19.34) * mm, "end": v(-15.62, 19.12) * mm});
            skLineSegment(sketch, "E665", {"start": v(-15.62, 19.12) * mm, "end": v(-15.3, 18.92) * mm});
            skLineSegment(sketch, "E666", {"start": v(-15.3, 18.92) * mm, "end": v(-15.04, 18.73) * mm});
            skLineSegment(sketch, "E667", {"start": v(-15.04, 18.73) * mm, "end": v(-14.92, 18.64) * mm});
            skArc(sketch, "E668", {"start": v(-14.92, 18.64) * mm, "mid": v(-14.66, 18.84) * mm, "end": v(-14.4, 19.05) * mm});
            skLineSegment(sketch, "E669", {"start": v(-14.4, 19.05) * mm, "end": v(-14.46, 19.18) * mm});
            skLineSegment(sketch, "E670", {"start": v(-14.46, 19.18) * mm, "end": v(-14.57, 19.48) * mm});
            skLineSegment(sketch, "E671", {"start": v(-14.57, 19.48) * mm, "end": v(-14.7, 19.84) * mm});
            skLineSegment(sketch, "E672", {"start": v(-14.7, 19.84) * mm, "end": v(-14.81, 20.26) * mm});
            skLineSegment(sketch, "E673", {"start": v(-14.81, 20.26) * mm, "end": v(-14.92, 20.74) * mm});
            skLineSegment(sketch, "E674", {"start": v(-14.92, 20.74) * mm, "end": v(-14.93, 20.8) * mm});
            skArc(sketch, "E675", {"start": v(-14.93, 20.8) * mm, "mid": v(-14.68, 20.98) * mm, "end": v(-14.41, 21.16) * mm});
            skLineSegment(sketch, "E676", {"start": v(-14.41, 21.16) * mm, "end": v(-14.37, 21.13) * mm});
            skLineSegment(sketch, "E677", {"start": v(-14.37, 21.13) * mm, "end": v(-13.96, 20.86) * mm});
            skLineSegment(sketch, "E678", {"start": v(-13.96, 20.86) * mm, "end": v(-13.6, 20.6) * mm});
            skLineSegment(sketch, "E679", {"start": v(-13.6, 20.6) * mm, "end": v(-13.3, 20.37) * mm});
            skLineSegment(sketch, "E680", {"start": v(-13.3, 20.37) * mm, "end": v(-13.07, 20.16) * mm});
            skLineSegment(sketch, "E681", {"start": v(-13.07, 20.16) * mm, "end": v(-12.96, 20.05) * mm});
            skArc(sketch, "E682", {"start": v(-12.96, 20.05) * mm, "mid": v(-12.68, 20.23) * mm, "end": v(-12.4, 20.4) * mm});
            skLineSegment(sketch, "E683", {"start": v(-12.4, 20.4) * mm, "end": v(-12.44, 20.55) * mm});
            skLineSegment(sketch, "E684", {"start": v(-12.44, 20.55) * mm, "end": v(-12.53, 20.86) * mm});
            skLineSegment(sketch, "E685", {"start": v(-12.53, 20.86) * mm, "end": v(-12.61, 21.23) * mm});
            skLineSegment(sketch, "E686", {"start": v(-12.61, 21.23) * mm, "end": v(-12.69, 21.66) * mm});
            skLineSegment(sketch, "E687", {"start": v(-12.69, 21.66) * mm, "end": v(-12.75, 22.15) * mm});
            skLineSegment(sketch, "E688", {"start": v(-12.75, 22.15) * mm, "end": v(-12.75, 22.2) * mm});
            skArc(sketch, "E689", {"start": v(-12.75, 22.2) * mm, "mid": v(-12.48, 22.35) * mm, "end": v(-12.2, 22.5) * mm});
            skLineSegment(sketch, "E690", {"start": v(-12.2, 22.5) * mm, "end": v(-12.16, 22.48) * mm});
            skLineSegment(sketch, "E691", {"start": v(-12.16, 22.48) * mm, "end": v(-11.77, 22.17) * mm});
            skLineSegment(sketch, "E692", {"start": v(-11.77, 22.17) * mm, "end": v(-11.45, 21.88) * mm});
            skLineSegment(sketch, "E693", {"start": v(-11.45, 21.88) * mm, "end": v(-11.18, 21.61) * mm});
            skLineSegment(sketch, "E694", {"start": v(-11.18, 21.61) * mm, "end": v(-10.96, 21.38) * mm});
            skLineSegment(sketch, "E695", {"start": v(-10.96, 21.38) * mm, "end": v(-10.86, 21.26) * mm});
            skArc(sketch, "E696", {"start": v(-10.86, 21.26) * mm, "mid": v(-10.57, 21.4) * mm, "end": v(-10.27, 21.55) * mm});
            skLineSegment(sketch, "E697", {"start": v(-10.27, 21.55) * mm, "end": v(-10.3, 21.7) * mm});
            skLineSegment(sketch, "E698", {"start": v(-10.3, 21.7) * mm, "end": v(-10.35, 22.02) * mm});
            skLineSegment(sketch, "E699", {"start": v(-10.35, 22.02) * mm, "end": v(-10.4, 22.4) * mm});
            skLineSegment(sketch, "E700", {"start": v(-10.4, 22.4) * mm, "end": v(-10.43, 22.83) * mm});
            skLineSegment(sketch, "E701", {"start": v(-10.43, 22.83) * mm, "end": v(-10.44, 23.32) * mm});
            skLineSegment(sketch, "E702", {"start": v(-10.44, 23.32) * mm, "end": v(-10.44, 23.37) * mm});
            skArc(sketch, "E703", {"start": v(-10.44, 23.37) * mm, "mid": v(-10.15, 23.5) * mm, "end": v(-9.86, 23.62) * mm});
            skLineSegment(sketch, "E704", {"start": v(-9.86, 23.62) * mm, "end": v(-9.82, 23.6) * mm});
            skLineSegment(sketch, "E705", {"start": v(-9.82, 23.6) * mm, "end": v(-9.47, 23.24) * mm});
            skLineSegment(sketch, "E706", {"start": v(-9.47, 23.24) * mm, "end": v(-9.18, 22.92) * mm});
            skLineSegment(sketch, "E707", {"start": v(-9.18, 22.92) * mm, "end": v(-8.93, 22.63) * mm});
            skLineSegment(sketch, "E708", {"start": v(-8.93, 22.63) * mm, "end": v(-8.74, 22.37) * mm});
            skLineSegment(sketch, "E709", {"start": v(-8.74, 22.37) * mm, "end": v(-8.66, 22.25) * mm});
            skArc(sketch, "E710", {"start": v(-8.66, 22.25) * mm, "mid": v(-8.35, 22.37) * mm, "end": v(-8.03, 22.48) * mm});
            skLineSegment(sketch, "E711", {"start": v(-8.03, 22.48) * mm, "end": v(-8.05, 22.63) * mm});
            skLineSegment(sketch, "E712", {"start": v(-8.05, 22.63) * mm, "end": v(-8.07, 22.95) * mm});
            skLineSegment(sketch, "E713", {"start": v(-8.07, 22.95) * mm, "end": v(-8.08, 23.33) * mm});
            skLineSegment(sketch, "E714", {"start": v(-8.08, 23.33) * mm, "end": v(-8.07, 23.77) * mm});
            skLineSegment(sketch, "E715", {"start": v(-8.07, 23.77) * mm, "end": v(-8.03, 24.26) * mm});
            skLineSegment(sketch, "E716", {"start": v(-8.03, 24.26) * mm, "end": v(-8.02, 24.31) * mm});
            skArc(sketch, "E717", {"start": v(-8.02, 24.31) * mm, "mid": v(-7.72, 24.4) * mm, "end": v(-7.42, 24.5) * mm});
            skLineSegment(sketch, "E718", {"start": v(-7.42, 24.5) * mm, "end": v(-7.39, 24.46) * mm});
            skLineSegment(sketch, "E719", {"start": v(-7.39, 24.46) * mm, "end": v(-7.07, 24.08) * mm});
            skLineSegment(sketch, "E720", {"start": v(-7.07, 24.08) * mm, "end": v(-6.8, 23.73) * mm});
            skLineSegment(sketch, "E721", {"start": v(-6.8, 23.73) * mm, "end": v(-6.6, 23.42) * mm});
            skLineSegment(sketch, "E722", {"start": v(-6.6, 23.42) * mm, "end": v(-6.43, 23.14) * mm});
            skLineSegment(sketch, "E723", {"start": v(-6.43, 23.14) * mm, "end": v(-6.36, 23.01) * mm});
            skArc(sketch, "E724", {"start": v(-6.36, 23.01) * mm, "mid": v(-6.04, 23.1) * mm, "end": v(-5.72, 23.18) * mm});
            skLineSegment(sketch, "E725", {"start": v(-5.72, 23.18) * mm, "end": v(-5.72, 23.33) * mm});
            skLineSegment(sketch, "E726", {"start": v(-5.72, 23.33) * mm, "end": v(-5.7, 23.65) * mm});
            skLineSegment(sketch, "E727", {"start": v(-5.7, 23.65) * mm, "end": v(-5.68, 24.03) * mm});
            skLineSegment(sketch, "E728", {"start": v(-5.68, 24.03) * mm, "end": v(-5.62, 24.46) * mm});
            skLineSegment(sketch, "E729", {"start": v(-5.62, 24.46) * mm, "end": v(-5.53, 24.95) * mm});
            skLineSegment(sketch, "E730", {"start": v(-5.53, 24.95) * mm, "end": v(-5.52, 25) * mm});
            skArc(sketch, "E731", {"start": v(-5.52, 25) * mm, "mid": v(-5.21, 25.06) * mm, "end": v(-4.9, 25.13) * mm});
            skLineSegment(sketch, "E732", {"start": v(-4.9, 25.13) * mm, "end": v(-4.87, 25.09) * mm});
            skLineSegment(sketch, "E733", {"start": v(-4.87, 25.09) * mm, "end": v(-4.6, 24.67) * mm});
            skLineSegment(sketch, "E734", {"start": v(-4.6, 24.67) * mm, "end": v(-4.37, 24.3) * mm});
            skLineSegment(sketch, "E735", {"start": v(-4.37, 24.3) * mm, "end": v(-4.2, 23.97) * mm});
            skLineSegment(sketch, "E736", {"start": v(-4.2, 23.97) * mm, "end": v(-4.06, 23.68) * mm});
            skLineSegment(sketch, "E737", {"start": v(-4.06, 23.68) * mm, "end": v(-4, 23.54) * mm});
            skArc(sketch, "E738", {"start": v(-4, 23.54) * mm, "mid": v(-3.67, 23.6) * mm, "end": v(-3.34, 23.64) * mm});
            skLineSegment(sketch, "E739", {"start": v(-3.34, 23.64) * mm, "end": v(-3.33, 23.79) * mm});
            skLineSegment(sketch, "E740", {"start": v(-3.33, 23.79) * mm, "end": v(-3.29, 24.1) * mm});
            skLineSegment(sketch, "E741", {"start": v(-3.29, 24.1) * mm, "end": v(-3.22, 24.48) * mm});
            skLineSegment(sketch, "E742", {"start": v(-3.22, 24.48) * mm, "end": v(-3.12, 24.9) * mm});
            skLineSegment(sketch, "E743", {"start": v(-3.12, 24.9) * mm, "end": v(-2.98, 25.38) * mm});
            skLineSegment(sketch, "E744", {"start": v(-2.98, 25.38) * mm, "end": v(-2.97, 25.43) * mm});
            skArc(sketch, "E745", {"start": v(-2.97, 25.43) * mm, "mid": v(-2.65, 25.46) * mm, "end": v(-2.34, 25.5) * mm});
            skLineSegment(sketch, "E746", {"start": v(-2.34, 25.5) * mm, "end": v(-2.31, 25.45) * mm});
            skLineSegment(sketch, "E747", {"start": v(-2.31, 25.45) * mm, "end": v(-2.08, 25.01) * mm});
            skLineSegment(sketch, "E748", {"start": v(-2.08, 25.01) * mm, "end": v(-1.9, 24.62) * mm});
            skLineSegment(sketch, "E749", {"start": v(-1.9, 24.62) * mm, "end": v(-1.75, 24.27) * mm});
            skLineSegment(sketch, "E750", {"start": v(-1.75, 24.27) * mm, "end": v(-1.64, 23.97) * mm});
            skLineSegment(sketch, "E751", {"start": v(-1.64, 23.97) * mm, "end": v(-1.6, 23.82) * mm});
            skArc(sketch, "E752", {"start": v(-1.6, 23.82) * mm, "mid": v(-1.27, 23.84) * mm, "end": v(-0.93, 23.86) * mm});
            skLineSegment(sketch, "E753", {"start": v(-0.93, 23.86) * mm, "end": v(-0.9, 24) * mm});
            skLineSegment(sketch, "E754", {"start": v(-0.9, 24) * mm, "end": v(-0.83, 24.32) * mm});
            skLineSegment(sketch, "E755", {"start": v(-0.83, 24.32) * mm, "end": v(-0.73, 24.68) * mm});
            skLineSegment(sketch, "E756", {"start": v(-0.73, 24.68) * mm, "end": v(-0.58, 25.1) * mm});
            skLineSegment(sketch, "E757", {"start": v(-0.58, 25.1) * mm, "end": v(-0.4, 25.55) * mm});
            skLineSegment(sketch, "E758", {"start": v(-0.4, 25.55) * mm, "end": v(-0.38, 25.6) * mm});
            skArc(sketch, "E759", {"start": v(-0.38, 25.6) * mm, "mid": v(-0.06, 25.6) * mm, "end": v(0.25, 25.6) * mm});
            skLineSegment(sketch, "E760", {"start": v(0.25, 25.6) * mm, "end": v(0.28, 25.55) * mm});
            skLineSegment(sketch, "E761", {"start": v(0.28, 25.55) * mm, "end": v(0.46, 25.1) * mm});
            skLineSegment(sketch, "E762", {"start": v(0.46, 25.1) * mm, "end": v(0.6, 24.68) * mm});
            skLineSegment(sketch, "E763", {"start": v(0.6, 24.68) * mm, "end": v(0.71, 24.32) * mm});
            skLineSegment(sketch, "E764", {"start": v(0.71, 24.32) * mm, "end": v(0.8, 24) * mm});
            skLineSegment(sketch, "E765", {"start": v(0.8, 24) * mm, "end": v(0.82, 23.86) * mm});
            skArc(sketch, "E766", {"start": v(0.82, 23.86) * mm, "mid": v(1.15, 23.85) * mm, "end": v(1.48, 23.83) * mm});
            skLineSegment(sketch, "E767", {"start": v(1.48, 23.83) * mm, "end": v(1.53, 23.97) * mm});
            skLineSegment(sketch, "E768", {"start": v(1.53, 23.97) * mm, "end": v(1.63, 24.28) * mm});
            skLineSegment(sketch, "E769", {"start": v(1.63, 24.28) * mm, "end": v(1.77, 24.63) * mm});
            skLineSegment(sketch, "E770", {"start": v(1.77, 24.63) * mm, "end": v(1.96, 25.02) * mm});
            skLineSegment(sketch, "E771", {"start": v(1.96, 25.02) * mm, "end": v(2.19, 25.46) * mm});
            skLineSegment(sketch, "E772", {"start": v(2.19, 25.46) * mm, "end": v(2.21, 25.5) * mm});
            skArc(sketch, "E773", {"start": v(2.21, 25.5) * mm, "mid": v(2.53, 25.47) * mm, "end": v(2.84, 25.44) * mm});
            skLineSegment(sketch, "E774", {"start": v(2.84, 25.44) * mm, "end": v(2.86, 25.4) * mm});
            skLineSegment(sketch, "E775", {"start": v(2.86, 25.4) * mm, "end": v(3, 24.92) * mm});
            skLineSegment(sketch, "E776", {"start": v(3, 24.92) * mm, "end": v(3.1, 24.5) * mm});
            skLineSegment(sketch, "E777", {"start": v(3.1, 24.5) * mm, "end": v(3.17, 24.12) * mm});
            skLineSegment(sketch, "E778", {"start": v(3.17, 24.12) * mm, "end": v(3.22, 23.8) * mm});
            skLineSegment(sketch, "E779", {"start": v(3.22, 23.8) * mm, "end": v(3.23, 23.66) * mm});
            skArc(sketch, "E780", {"start": v(3.23, 23.66) * mm, "mid": v(3.56, 23.6) * mm, "end": v(3.89, 23.56) * mm});
            skLineSegment(sketch, "E781", {"start": v(3.89, 23.56) * mm, "end": v(3.94, 23.7) * mm});
            skLineSegment(sketch, "E782", {"start": v(3.94, 23.7) * mm, "end": v(4.08, 23.99) * mm});
            skLineSegment(sketch, "E783", {"start": v(4.08, 23.99) * mm, "end": v(4.26, 24.32) * mm});
            skLineSegment(sketch, "E784", {"start": v(4.26, 24.32) * mm, "end": v(4.48, 24.7) * mm});
            skLineSegment(sketch, "E785", {"start": v(4.48, 24.7) * mm, "end": v(4.75, 25.1) * mm});
            skLineSegment(sketch, "E786", {"start": v(4.75, 25.1) * mm, "end": v(4.78, 25.15) * mm});
            skArc(sketch, "E787", {"start": v(4.78, 25.15) * mm, "mid": v(5.1, 25.09) * mm, "end": v(5.4, 25.02) * mm});
            skLineSegment(sketch, "E788", {"start": v(5.4, 25.02) * mm, "end": v(5.41, 24.98) * mm});
            skLineSegment(sketch, "E789", {"start": v(5.41, 24.98) * mm, "end": v(5.5, 24.49) * mm});
            skLineSegment(sketch, "E790", {"start": v(5.5, 24.49) * mm, "end": v(5.56, 24.06) * mm});
            skLineSegment(sketch, "E791", {"start": v(5.56, 24.06) * mm, "end": v(5.6, 23.68) * mm});
            skLineSegment(sketch, "E792", {"start": v(5.6, 23.68) * mm, "end": v(5.6, 23.36) * mm});
            skLineSegment(sketch, "E793", {"start": v(5.6, 23.36) * mm, "end": v(5.6, 23.2) * mm});
            skArc(sketch, "E794", {"start": v(5.6, 23.2) * mm, "mid": v(5.93, 23.13) * mm, "end": v(6.25, 23.04) * mm});
            skLineSegment(sketch, "E795", {"start": v(6.25, 23.04) * mm, "end": v(6.32, 23.17) * mm});
            skLineSegment(sketch, "E796", {"start": v(6.32, 23.17) * mm, "end": v(6.49, 23.45) * mm});
            skLineSegment(sketch, "E797", {"start": v(6.49, 23.45) * mm, "end": v(6.7, 23.77) * mm});
            skLineSegment(sketch, "E798", {"start": v(6.7, 23.77) * mm, "end": v(6.96, 24.12) * mm});
            skLineSegment(sketch, "E799", {"start": v(6.96, 24.12) * mm, "end": v(7.27, 24.5) * mm});
            skLineSegment(sketch, "E800", {"start": v(7.27, 24.5) * mm, "end": v(7.3, 24.54) * mm});
            skArc(sketch, "E801", {"start": v(7.3, 24.54) * mm, "mid": v(7.6, 24.44) * mm, "end": v(7.9, 24.35) * mm});
            skLineSegment(sketch, "E802", {"start": v(7.9, 24.35) * mm, "end": v(7.91, 24.3) * mm});
            skLineSegment(sketch, "E803", {"start": v(7.91, 24.3) * mm, "end": v(7.95, 23.8) * mm});
            skLineSegment(sketch, "E804", {"start": v(7.95, 23.8) * mm, "end": v(7.97, 23.37) * mm});
            skLineSegment(sketch, "E805", {"start": v(7.97, 23.37) * mm, "end": v(7.96, 23) * mm});
            skLineSegment(sketch, "E806", {"start": v(7.96, 23) * mm, "end": v(7.94, 22.67) * mm});
            skLineSegment(sketch, "E807", {"start": v(7.94, 22.67) * mm, "end": v(7.92, 22.52) * mm});
            skArc(sketch, "E808", {"start": v(7.92, 22.52) * mm, "mid": v(8.24, 22.4) * mm, "end": v(8.55, 22.3) * mm});
            skLineSegment(sketch, "E809", {"start": v(8.55, 22.3) * mm, "end": v(8.63, 22.42) * mm});
            skLineSegment(sketch, "E810", {"start": v(8.63, 22.42) * mm, "end": v(8.82, 22.67) * mm});
            skLineSegment(sketch, "E811", {"start": v(8.82, 22.67) * mm, "end": v(9.07, 22.97) * mm});
            skLineSegment(sketch, "E812", {"start": v(9.07, 22.97) * mm, "end": v(9.36, 23.29) * mm});
            skLineSegment(sketch, "E813", {"start": v(9.36, 23.29) * mm, "end": v(9.71, 23.64) * mm});
            skLineSegment(sketch, "E814", {"start": v(9.71, 23.64) * mm, "end": v(9.75, 23.67) * mm});
            skArc(sketch, "E815", {"start": v(9.75, 23.67) * mm, "mid": v(10.04, 23.55) * mm, "end": v(10.33, 23.42) * mm});
            skLineSegment(sketch, "E816", {"start": v(10.33, 23.42) * mm, "end": v(10.33, 23.37) * mm});
            skLineSegment(sketch, "E817", {"start": v(10.33, 23.37) * mm, "end": v(10.32, 22.88) * mm});
            skLineSegment(sketch, "E818", {"start": v(10.32, 22.88) * mm, "end": v(10.3, 22.44) * mm});
            skLineSegment(sketch, "E819", {"start": v(10.3, 22.44) * mm, "end": v(10.25, 22.07) * mm});
            skLineSegment(sketch, "E820", {"start": v(10.25, 22.07) * mm, "end": v(10.2, 21.75) * mm});
            skLineSegment(sketch, "E821", {"start": v(10.2, 21.75) * mm, "end": v(10.16, 21.6) * mm});
            skArc(sketch, "E822", {"start": v(10.16, 21.6) * mm, "mid": v(10.46, 21.46) * mm, "end": v(10.76, 21.31) * mm});
            skLineSegment(sketch, "E823", {"start": v(10.76, 21.31) * mm, "end": v(10.86, 21.43) * mm});
            skLineSegment(sketch, "E824", {"start": v(10.86, 21.43) * mm, "end": v(11.07, 21.66) * mm});
            skLineSegment(sketch, "E825", {"start": v(11.07, 21.66) * mm, "end": v(11.34, 21.93) * mm});
            skLineSegment(sketch, "E826", {"start": v(11.34, 21.93) * mm, "end": v(11.67, 22.22) * mm});
            skLineSegment(sketch, "E827", {"start": v(11.67, 22.22) * mm, "end": v(12.05, 22.53) * mm});
            skLineSegment(sketch, "E828", {"start": v(12.05, 22.53) * mm, "end": v(12.1, 22.56) * mm});
            skArc(sketch, "E829", {"start": v(12.1, 22.56) * mm, "mid": v(12.37, 22.41) * mm, "end": v(12.65, 22.26) * mm});
            skLineSegment(sketch, "E830", {"start": v(12.65, 22.26) * mm, "end": v(12.64, 22.2) * mm});
            skLineSegment(sketch, "E831", {"start": v(12.64, 22.2) * mm, "end": v(12.58, 21.72) * mm});
            skLineSegment(sketch, "E832", {"start": v(12.58, 21.72) * mm, "end": v(12.5, 21.29) * mm});
            skLineSegment(sketch, "E833", {"start": v(12.5, 21.29) * mm, "end": v(12.43, 20.92) * mm});
            skLineSegment(sketch, "E834", {"start": v(12.43, 20.92) * mm, "end": v(12.34, 20.6) * mm});
            skLineSegment(sketch, "E835", {"start": v(12.34, 20.6) * mm, "end": v(12.3, 20.47) * mm});
            skArc(sketch, "E836", {"start": v(12.3, 20.47) * mm, "mid": v(12.58, 20.3) * mm, "end": v(12.86, 20.11) * mm});
            skLineSegment(sketch, "E837", {"start": v(12.86, 20.11) * mm, "end": v(12.97, 20.22) * mm});
            skLineSegment(sketch, "E838", {"start": v(12.97, 20.22) * mm, "end": v(13.2, 20.43) * mm});
            skLineSegment(sketch, "E839", {"start": v(13.2, 20.43) * mm, "end": v(13.5, 20.67) * mm});
            skLineSegment(sketch, "E840", {"start": v(13.5, 20.67) * mm, "end": v(13.86, 20.93) * mm});
            skLineSegment(sketch, "E841", {"start": v(13.86, 20.93) * mm, "end": v(14.27, 21.2) * mm});
            skLineSegment(sketch, "E842", {"start": v(14.27, 21.2) * mm, "end": v(14.31, 21.23) * mm});
            skArc(sketch, "E843", {"start": v(14.31, 21.23) * mm, "mid": v(14.57, 21.05) * mm, "end": v(14.83, 20.87) * mm});
            skLineSegment(sketch, "E844", {"start": v(14.83, 20.87) * mm, "end": v(14.82, 20.82) * mm});
            skLineSegment(sketch, "E845", {"start": v(14.82, 20.82) * mm, "end": v(14.72, 20.33) * mm});
            skLineSegment(sketch, "E846", {"start": v(14.72, 20.33) * mm, "end": v(14.6, 19.91) * mm});
            skLineSegment(sketch, "E847", {"start": v(14.6, 19.91) * mm, "end": v(14.48, 19.55) * mm});
            skLineSegment(sketch, "E848", {"start": v(14.48, 19.55) * mm, "end": v(14.36, 19.25) * mm});
            skLineSegment(sketch, "E849", {"start": v(14.36, 19.25) * mm, "end": v(14.3, 19.12) * mm});
            skArc(sketch, "E850", {"start": v(14.3, 19.12) * mm, "mid": v(14.57, 18.91) * mm, "end": v(14.83, 18.7) * mm});
            skLineSegment(sketch, "E851", {"start": v(14.83, 18.7) * mm, "end": v(14.95, 18.8) * mm});
            skLineSegment(sketch, "E852", {"start": v(14.95, 18.8) * mm, "end": v(15.2, 19) * mm});
            skLineSegment(sketch, "E853", {"start": v(15.2, 19) * mm, "end": v(15.52, 19.2) * mm});
            skLineSegment(sketch, "E854", {"start": v(15.52, 19.2) * mm, "end": v(15.9, 19.42) * mm});
            skLineSegment(sketch, "E855", {"start": v(15.9, 19.42) * mm, "end": v(16.34, 19.65) * mm});
            skLineSegment(sketch, "E856", {"start": v(16.34, 19.65) * mm, "end": v(16.39, 19.67) * mm});
            skArc(sketch, "E857", {"start": v(16.39, 19.67) * mm, "mid": v(16.63, 19.46) * mm, "end": v(16.87, 19.26) * mm});
            skLineSegment(sketch, "E858", {"start": v(16.87, 19.26) * mm, "end": v(16.85, 19.2) * mm});
            skLineSegment(sketch, "E859", {"start": v(16.85, 19.2) * mm, "end": v(16.7, 18.74) * mm});
            skLineSegment(sketch, "E860", {"start": v(16.7, 18.74) * mm, "end": v(16.54, 18.33) * mm});
            skLineSegment(sketch, "E861", {"start": v(16.54, 18.33) * mm, "end": v(16.38, 17.99) * mm});
            skLineSegment(sketch, "E862", {"start": v(16.38, 17.99) * mm, "end": v(16.24, 17.7) * mm});
            skLineSegment(sketch, "E863", {"start": v(16.24, 17.7) * mm, "end": v(16.16, 17.57) * mm});
            skArc(sketch, "E864", {"start": v(16.16, 17.57) * mm, "mid": v(16.4, 17.34) * mm, "end": v(16.65, 17.11) * mm});
            skLineSegment(sketch, "E865", {"start": v(16.65, 17.11) * mm, "end": v(16.77, 17.2) * mm});
            skLineSegment(sketch, "E866", {"start": v(16.77, 17.2) * mm, "end": v(17.05, 17.36) * mm});
            skLineSegment(sketch, "E867", {"start": v(17.05, 17.36) * mm, "end": v(17.39, 17.53) * mm});
            skLineSegment(sketch, "E868", {"start": v(17.39, 17.53) * mm, "end": v(17.79, 17.71) * mm});
            skLineSegment(sketch, "E869", {"start": v(17.79, 17.71) * mm, "end": v(18.25, 17.9) * mm});
            skLineSegment(sketch, "E870", {"start": v(18.25, 17.9) * mm, "end": v(18.3, 17.9) * mm});
            skArc(sketch, "E871", {"start": v(18.3, 17.9) * mm, "mid": v(18.51, 17.68) * mm, "end": v(18.73, 17.45) * mm});
            skLineSegment(sketch, "E872", {"start": v(18.73, 17.45) * mm, "end": v(18.71, 17.4) * mm});
            skLineSegment(sketch, "E873", {"start": v(18.71, 17.4) * mm, "end": v(18.5, 16.95) * mm});
            skLineSegment(sketch, "E874", {"start": v(18.5, 16.95) * mm, "end": v(18.3, 16.57) * mm});
            skLineSegment(sketch, "E875", {"start": v(18.3, 16.57) * mm, "end": v(18.12, 16.24) * mm});
            skLineSegment(sketch, "E876", {"start": v(18.12, 16.24) * mm, "end": v(17.95, 15.97) * mm});
            skLineSegment(sketch, "E877", {"start": v(17.95, 15.97) * mm, "end": v(17.86, 15.85) * mm});
            skArc(sketch, "E878", {"start": v(17.86, 15.85) * mm, "mid": v(18.08, 15.6) * mm, "end": v(18.3, 15.34) * mm});
            skCircle(sketch, "E879", {"center": v(-15, 0) * mm, "radius": 6 * mm});
            skCircle(sketch, "E880", {"center": v(0, 15) * mm, "radius": 6 * mm});
            skCircle(sketch, "E881", {"center": v(15, 0) * mm, "radius": 6 * mm});
            skCircle(sketch, "E882", {"center": v(0, -15) * mm, "radius": 6 * mm});
            skSolve(sketch);
        }
        {
            var Q0;
            Q0=makeQuery(id+"F6.imprint","IMPRINT",FACE,{"disambiguationData":[TD([[makeQuery(id+"F6.imprint","IMPRINT",EDGE,{"derivedFrom":sQuery(id+"F6.wireOp",EDGE,"E11")}),-1.0]])]});
            extrude(context, id + "F7", {"entities" : qUnion([Q0]), "operationType" : NewBodyOperationType.ADD, "depth" : 6 * mm});
        }
        {
            var Q0;
            Q0=makeQuery(id+"F0.imprint","IMPRINT",FACE,{"disambiguationData":[TD([[makeQuery(id+"F0.imprint","IMPRINT",EDGE,{"derivedFrom":sQuery(id+"F0.wireOp",EDGE,"E0")}),-1.0]])]});
            extrude(context, id + "F8", {"entities" : qUnion([Q0]), "operationType" : NewBodyOperationType.REMOVE, "depth" : 10 * mm});
        }
    });
